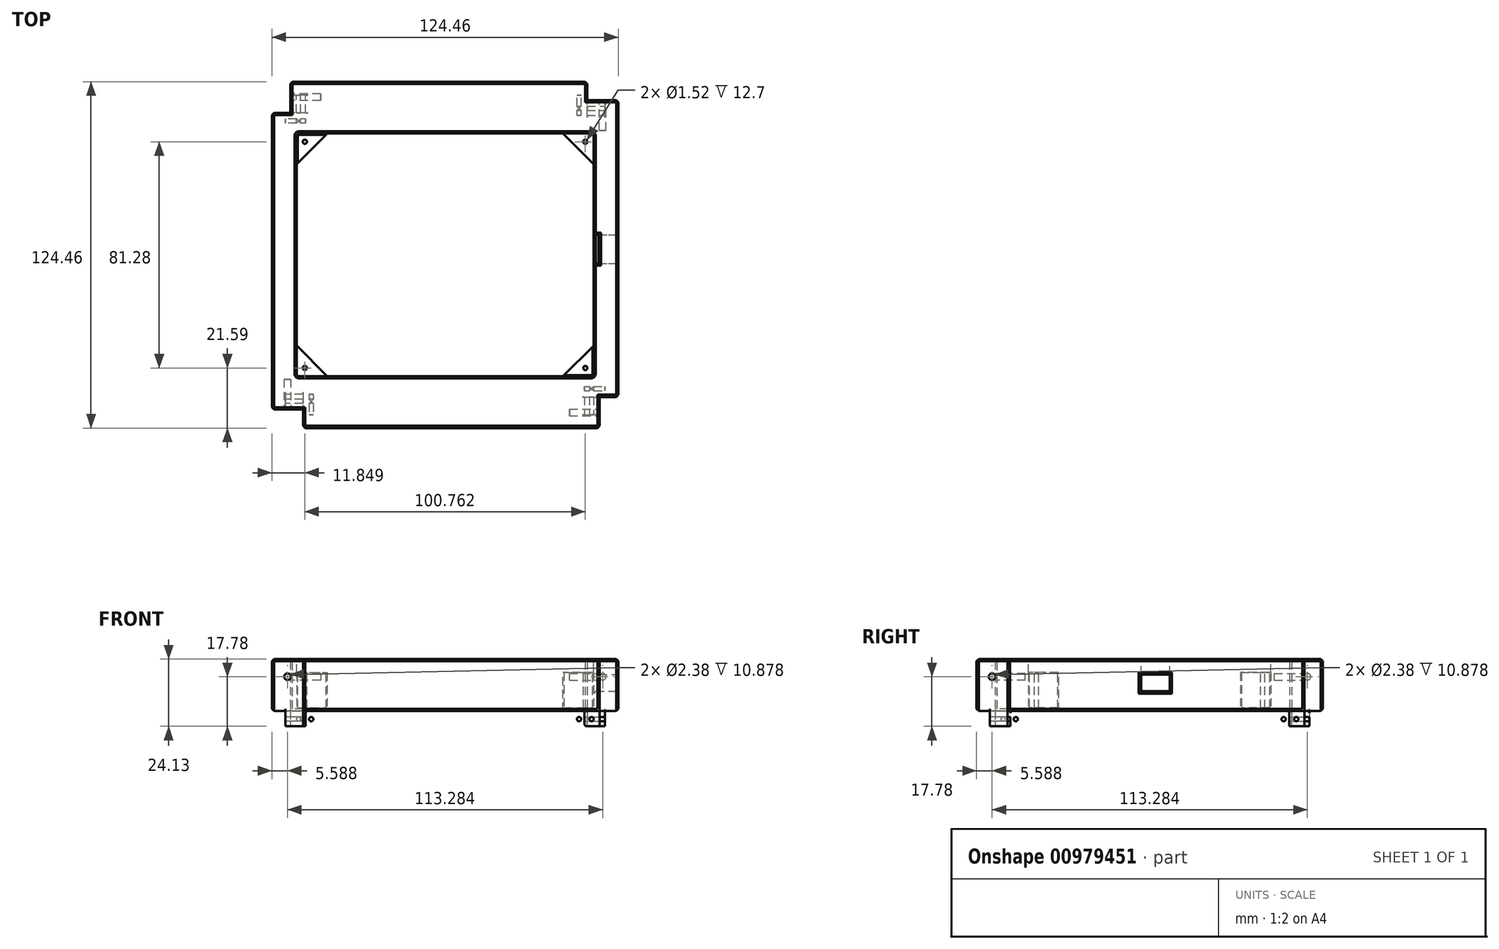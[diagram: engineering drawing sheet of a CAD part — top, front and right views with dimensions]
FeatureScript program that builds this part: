
annotation { "Feature Type Name" : "Feature", "Feature Type Description" : "" }
export const myFeature = defineFeature(function(context is Context, id is Id, definition is map)
    precondition{}
    {
        {
            var Q0;
            Q0=qCreatedBy(makeId("Top.planeOp"),FACE);
            var sketch = newSketch(context, id + "F0", { "sketchPlane" : qUnion([Q0])});
            skLineSegment(sketch, "E0.bottom", {"start": v(62.23, -62.23) * mm, "end": v(-62.23, -62.23) * mm});
            skLineSegment(sketch, "E0.top", {"start": v(62.23, 62.23) * mm, "end": v(-62.23, 62.23) * mm});
            skLineSegment(sketch, "E0.left", {"start": v(62.23, -62.23) * mm, "end": v(62.23, 62.23) * mm});
            skLineSegment(sketch, "E0.right", {"start": v(-62.23, -62.23) * mm, "end": v(-62.23, 62.23) * mm});
            skLineSegment(sketch, "E1.bottom", {"start": v(38.1, -38.1) * mm, "end": v(-38.1, -38.1) * mm});
            skLineSegment(sketch, "E1.top", {"start": v(38.1, 38.1) * mm, "end": v(-38.1, 38.1) * mm});
            skLineSegment(sketch, "E1.left", {"start": v(38.1, -38.1) * mm, "end": v(38.1, 38.1) * mm});
            skLineSegment(sketch, "E1.right", {"start": v(-38.1, -38.1) * mm, "end": v(-38.1, 38.1) * mm});
            skPoint(sketch, "E1.middle", {"position": v(0, 0) * mm});
            skSolve(sketch);
        }
        {
            var Q0;
            Q0=makeQuery(id+"F0.imprint","IMPRINT",FACE,{"disambiguationData":[TD([[makeQuery(id+"F0.imprint","IMPRINT",EDGE,{"derivedFrom":sQuery(id+"F0.wireOp",EDGE,"E0.bottom")}),-1.0]])]});
            extrude(context, id + "F1", {"entities" : qUnion([Q0]), "depth" : 124.46 * mm, "offsetDistance" : 25.4 * mm});
        }
        {
            var Q0;
            Q0=makeQuery(id+"F1.opExtrude","CAP_FACE",FACE,{"disambiguationData":[OSD([sQuery(id+"F0.wireOp",EDGE,"E0.bottom"),sQuery(id+"F0.wireOp",EDGE,"E0.top"),sQuery(id+"F0.wireOp",EDGE,"E0.left"),sQuery(id+"F0.wireOp",EDGE,"E0.right")])],"isStart":false});
            var sketch = newSketch(context, id + "F2", { "sketchPlane" : qUnion([Q0])});
            skLineSegment(sketch, "E2.bottom", {"start": v(-52.92, 43.18) * mm, "end": v(52.92, 43.18) * mm});
            skLineSegment(sketch, "E2.top", {"start": v(-52.92, -43.18) * mm, "end": v(52.92, -43.18) * mm});
            skLineSegment(sketch, "E2.left", {"start": v(-52.92, 43.18) * mm, "end": v(-52.92, -43.18) * mm});
            skLineSegment(sketch, "E2.right", {"start": v(52.92, 43.18) * mm, "end": v(52.92, -43.18) * mm});
            skPoint(sketch, "E2.middle", {"position": v(0, 0) * mm});
            skCircle(sketch, "E3", {"center": v(-50.38, -40.64) * mm, "radius": 0.76 * mm});
            skCircle(sketch, "E4.MirrorC", {"center": v(50.38, -40.64) * mm, "radius": 0.76 * mm});
            skCircle(sketch, "E5.MirrorC", {"center": v(-50.38, 40.64) * mm, "radius": 0.76 * mm});
            skCircle(sketch, "E6.MirrorC", {"center": v(50.38, 40.64) * mm, "radius": 0.76 * mm});
            skLineSegment(sketch, "E7.0", {"start": v(-53.32, 43.58) * mm, "end": v(-53.32, -43.58) * mm});
            skLineSegment(sketch, "E7.1", {"start": v(-53.32, 43.58) * mm, "end": v(53.32, 43.58) * mm});
            skLineSegment(sketch, "E7.2", {"start": v(53.32, 43.58) * mm, "end": v(53.32, -43.58) * mm});
            skLineSegment(sketch, "E7.3", {"start": v(-53.32, -43.58) * mm, "end": v(53.32, -43.58) * mm});
            skLineSegment(sketch, "E8.top", {"start": v(53.32, -38.1) * mm, "end": v(47.84, -38.1) * mm});
            skLineSegment(sketch, "E8.right", {"start": v(47.84, -43.58) * mm, "end": v(47.84, -38.1) * mm});
            skLineSegment(sketch, "E9.MirrorCS", {"start": v(47.84, 43.58) * mm, "end": v(47.84, 38.1) * mm});
            skLineSegment(sketch, "E10.MirrorCS", {"start": v(53.32, 38.1) * mm, "end": v(47.84, 38.1) * mm});
            skLineSegment(sketch, "E11.MirrorCS", {"start": v(-53.32, -38.1) * mm, "end": v(-47.84, -38.1) * mm});
            skLineSegment(sketch, "E12.MirrorCS", {"start": v(-47.84, -43.58) * mm, "end": v(-47.84, -38.1) * mm});
            skLineSegment(sketch, "E13.MirrorCS", {"start": v(-53.32, 38.1) * mm, "end": v(-47.84, 38.1) * mm});
            skLineSegment(sketch, "E14.MirrorCS", {"start": v(-47.84, 43.58) * mm, "end": v(-47.84, 38.1) * mm});
            skLineSegment(sketch, "E15.MirrorCS", {"start": v(51.04, 6.8) * mm, "end": v(54.8, 6.8) * mm});
            skLineSegment(sketch, "E16.MirrorCS", {"start": v(51.04, -3.13) * mm, "end": v(55.2, -3.13) * mm});
            skLineSegment(sketch, "E17.MirrorCS", {"start": v(51.04, -2.73) * mm, "end": v(54.8, -2.73) * mm});
            skLineSegment(sketch, "E18.MirrorCS", {"start": v(55.2, 7.2) * mm, "end": v(55.2, -3.13) * mm});
            skLineSegment(sketch, "E19.MirrorCS", {"start": v(51.04, 7.2) * mm, "end": v(55.2, 7.2) * mm});
            skLineSegment(sketch, "E20.MirrorCS", {"start": v(54.8, 6.8) * mm, "end": v(54.8, -2.73) * mm});
            skPoint(sketch, "E21.MirrorP", {"position": v(52.92, 2.03) * mm});
            skLineSegment(sketch, "E22.bottom", {"start": v(-62.23, -62.23) * mm, "end": v(62.23, -62.23) * mm});
            skLineSegment(sketch, "E22.top", {"start": v(-62.23, 62.23) * mm, "end": v(62.23, 62.23) * mm});
            skLineSegment(sketch, "E22.left", {"start": v(-62.23, -62.23) * mm, "end": v(-62.23, 62.23) * mm});
            skLineSegment(sketch, "E22.right", {"start": v(62.23, -62.23) * mm, "end": v(62.23, 62.23) * mm});
            skSolve(sketch);
        }
        {
            var Q0;
            Q0=makeQuery(id+"F2.imprint","IMPRINT",FACE,{"disambiguationData":[TD([[makeQuery(id+"F2.imprint","IMPRINT",EDGE,{"derivedFrom":sQuery(id+"F2.wireOp",EDGE,"E3")}),-1.0]])]});
            var Q1;
            {var subQ5=sQuery(id+"F2.wireOp",EDGE,"E2.left");var subQ6=sQuery(id+"F2.wireOp",EDGE,"E2.top");var subQ7=makeQuery(id+"F2.imprint","INTERSECT",VERTEX,{"derivedFrom":[subQ6,subQ5]});Q1=makeQuery(id+"F2.imprint","IMPRINT",FACE,{"disambiguationData":[TD([[makeQuery(id+"F2.imprint","IMPRINT",EDGE,{"disambiguationData":[TD([[subQ7,-1.0]])],"derivedFrom":subQ6}),-1.0]])]});}
            var Q2;
            {var subQ7=sQuery(id+"F2.wireOp",EDGE,"E2.right");var subQ8=sQuery(id+"F2.wireOp",EDGE,"E2.top");var subQ9=makeQuery(id+"F2.imprint","INTERSECT",VERTEX,{"derivedFrom":[subQ8,subQ7]});Q2=makeQuery(id+"F2.imprint","IMPRINT",FACE,{"disambiguationData":[TD([[makeQuery(id+"F2.imprint","IMPRINT",EDGE,{"disambiguationData":[TD([[subQ9,1.0]])],"derivedFrom":subQ8}),-1.0]])]});}
            var Q3;
            Q3=makeQuery(id+"F2.imprint","IMPRINT",FACE,{"disambiguationData":[TD([[makeQuery(id+"F2.imprint","IMPRINT",EDGE,{"derivedFrom":sQuery(id+"F2.wireOp",EDGE,"E4.MirrorC")}),1.0]])]});
            var Q4;
            {var subQ7=sQuery(id+"F2.wireOp",EDGE,"E2.right");var subQ8=sQuery(id+"F2.wireOp",EDGE,"E2.bottom");var subQ9=makeQuery(id+"F2.imprint","INTERSECT",VERTEX,{"derivedFrom":[subQ8,subQ7]});Q4=makeQuery(id+"F2.imprint","IMPRINT",FACE,{"disambiguationData":[TD([[makeQuery(id+"F2.imprint","IMPRINT",EDGE,{"disambiguationData":[TD([[subQ9,1.0]])],"derivedFrom":subQ8}),1.0]])]});}
            var Q5;
            Q5=makeQuery(id+"F2.imprint","IMPRINT",FACE,{"disambiguationData":[TD([[makeQuery(id+"F2.imprint","IMPRINT",EDGE,{"derivedFrom":sQuery(id+"F2.wireOp",EDGE,"E6.MirrorC")}),-1.0]])]});
            var Q6;
            {var subQ5=sQuery(id+"F2.wireOp",EDGE,"E2.left");var subQ6=sQuery(id+"F2.wireOp",EDGE,"E2.bottom");var subQ7=makeQuery(id+"F2.imprint","INTERSECT",VERTEX,{"derivedFrom":[subQ6,subQ5]});Q6=makeQuery(id+"F2.imprint","IMPRINT",FACE,{"disambiguationData":[TD([[makeQuery(id+"F2.imprint","IMPRINT",EDGE,{"disambiguationData":[TD([[subQ7,-1.0]])],"derivedFrom":subQ6}),1.0]])]});}
            var Q7;
            Q7=makeQuery(id+"F2.imprint","IMPRINT",FACE,{"disambiguationData":[TD([[makeQuery(id+"F2.imprint","IMPRINT",EDGE,{"derivedFrom":sQuery(id+"F2.wireOp",EDGE,"E5.MirrorC")}),1.0]])]});
            extrude(context, id + "F3", {"entities" : qUnion([Q0, Q1, Q2, Q3, Q4, Q5, Q6, Q7]), "operationType" : NewBodyOperationType.REMOVE, "oppositeDirection" : true, "depth" : 4.83 * mm, "offsetDistance" : 25.4 * mm});
        }
        {
            var Q0;
            {var subQ20=sQuery(id+"F2.wireOp",EDGE,"E2.bottom");var subQ22=sQuery(id+"F2.wireOp",EDGE,"E14.MirrorCS");var subQ23=makeQuery(id+"F2.imprint","INTERSECT",VERTEX,{"derivedFrom":[subQ20,subQ22]});Q0=makeQuery(id+"F2.imprint","IMPRINT",FACE,{"disambiguationData":[TD([[makeQuery(id+"F2.imprint","IMPRINT",EDGE,{"disambiguationData":[TD([[subQ23,-1.0]])],"derivedFrom":subQ20}),-1.0]])]});}
            var Q1;
            {var subQ0=sQuery(id+"F2.wireOp",EDGE,"E14.MirrorCS");var subQ1=sQuery(id+"F2.wireOp",EDGE,"E2.bottom");var subQ2=makeQuery(id+"F2.imprint","INTERSECT",VERTEX,{"derivedFrom":[subQ1,subQ0]});Q1=makeQuery(id+"F2.imprint","IMPRINT",FACE,{"disambiguationData":[TD([[makeQuery(id+"F2.imprint","IMPRINT",EDGE,{"disambiguationData":[TD([[subQ2,-1.0]])],"derivedFrom":subQ1}),1.0]])]});}
            var Q2;
            {var subQ0=sQuery(id+"F2.wireOp",EDGE,"59694670-6818-448a-b48b-58002c6f26f5.2");var subQ1=sQuery(id+"F2.wireOp",EDGE,"E2.left");var subQ2=makeQuery(id+"F2.imprint","INTERSECT",VERTEX,{"derivedFrom":[subQ1,subQ0]});Q2=makeQuery(id+"F2.imprint","IMPRINT",FACE,{"disambiguationData":[TD([[makeQuery(id+"F2.imprint","IMPRINT",EDGE,{"disambiguationData":[TD([[subQ2,1.0]])],"derivedFrom":subQ1}),-1.0]])]});}
            var Q3;
            {var subQ0=sQuery(id+"F2.wireOp",EDGE,"E10.MirrorCS");var subQ1=sQuery(id+"F2.wireOp",EDGE,"E2.right");var subQ2=makeQuery(id+"F2.imprint","INTERSECT",VERTEX,{"derivedFrom":[subQ1,subQ0]});Q3=makeQuery(id+"F2.imprint","IMPRINT",FACE,{"disambiguationData":[TD([[makeQuery(id+"F2.imprint","IMPRINT",EDGE,{"disambiguationData":[TD([[subQ2,-1.0]])],"derivedFrom":subQ1}),1.0]])]});}
            var Q4;
            {var subQ0=sQuery(id+"F2.wireOp",EDGE,"E12.MirrorCS");var subQ1=sQuery(id+"F2.wireOp",EDGE,"E2.top");var subQ2=makeQuery(id+"F2.imprint","INTERSECT",VERTEX,{"derivedFrom":[subQ1,subQ0]});Q4=makeQuery(id+"F2.imprint","IMPRINT",FACE,{"disambiguationData":[TD([[makeQuery(id+"F2.imprint","IMPRINT",EDGE,{"disambiguationData":[TD([[subQ2,-1.0]])],"derivedFrom":subQ1}),-1.0]])]});}
            var Q5;
            {var subQ0=sQuery(id+"F2.wireOp",EDGE,"01Z94Qzt-EJPi-t4h5-vXe4-wsMJar4ZymQo.bottom");var subQ1=sQuery(id+"F2.wireOp",EDGE,"E2.left");var subQ2=makeQuery(id+"F2.imprint","INTERSECT",VERTEX,{"derivedFrom":[subQ1,subQ0]});Q5=makeQuery(id+"F2.imprint","IMPRINT",FACE,{"disambiguationData":[TD([[makeQuery(id+"F2.imprint","IMPRINT",EDGE,{"disambiguationData":[TD([[subQ2,-1.0]])],"derivedFrom":subQ1}),-1.0]])]});}
            var Q6;
            {var subQ0=sQuery(id+"F2.wireOp",EDGE,"59694670-6818-448a-b48b-58002c6f26f5.2");var subQ1=sQuery(id+"F2.wireOp",EDGE,"E2.left");var subQ2=makeQuery(id+"F2.imprint","INTERSECT",VERTEX,{"derivedFrom":[subQ1,subQ0]});Q6=makeQuery(id+"F2.imprint","IMPRINT",FACE,{"disambiguationData":[TD([[makeQuery(id+"F2.imprint","IMPRINT",EDGE,{"disambiguationData":[TD([[subQ2,-1.0]])],"derivedFrom":subQ1}),-1.0]])]});}
            var Q7;
            {var subQ0=sQuery(id+"F2.wireOp",EDGE,"01Z94Qzt-EJPi-t4h5-vXe4-wsMJar4ZymQo.top");var subQ1=sQuery(id+"F2.wireOp",EDGE,"E2.left");var subQ2=makeQuery(id+"F2.imprint","INTERSECT",VERTEX,{"derivedFrom":[subQ1,subQ0]});Q7=makeQuery(id+"F2.imprint","IMPRINT",FACE,{"disambiguationData":[TD([[makeQuery(id+"F2.imprint","IMPRINT",EDGE,{"disambiguationData":[TD([[subQ2,-1.0]])],"derivedFrom":subQ1}),-1.0]])]});}
            var Q8;
            {var subQ0=sQuery(id+"F2.wireOp",EDGE,"59694670-6818-448a-b48b-58002c6f26f5.0");var subQ1=sQuery(id+"F2.wireOp",EDGE,"E2.left");var subQ2=makeQuery(id+"F2.imprint","INTERSECT",VERTEX,{"derivedFrom":[subQ1,subQ0]});Q8=makeQuery(id+"F2.imprint","IMPRINT",FACE,{"disambiguationData":[TD([[makeQuery(id+"F2.imprint","IMPRINT",EDGE,{"disambiguationData":[TD([[subQ2,-1.0]])],"derivedFrom":subQ1}),-1.0]])]});}
            var Q9;
            {var subQ0=sQuery(id+"F2.wireOp",EDGE,"E19.MirrorCS");var subQ1=sQuery(id+"F2.wireOp",EDGE,"E2.right");var subQ2=makeQuery(id+"F2.imprint","INTERSECT",VERTEX,{"derivedFrom":[subQ1,subQ0]});Q9=makeQuery(id+"F2.imprint","IMPRINT",FACE,{"disambiguationData":[TD([[makeQuery(id+"F2.imprint","IMPRINT",EDGE,{"disambiguationData":[TD([[subQ2,-1.0]])],"derivedFrom":subQ1}),1.0]])]});}
            var Q10;
            {var subQ0=sQuery(id+"F2.wireOp",EDGE,"E15.MirrorCS");var subQ1=sQuery(id+"F2.wireOp",EDGE,"E2.right");var subQ2=makeQuery(id+"F2.imprint","INTERSECT",VERTEX,{"derivedFrom":[subQ1,subQ0]});Q10=makeQuery(id+"F2.imprint","IMPRINT",FACE,{"disambiguationData":[TD([[makeQuery(id+"F2.imprint","IMPRINT",EDGE,{"disambiguationData":[TD([[subQ2,-1.0]])],"derivedFrom":subQ1}),1.0]])]});}
            var Q11;
            {var subQ0=sQuery(id+"F2.wireOp",EDGE,"E17.MirrorCS");var subQ1=sQuery(id+"F2.wireOp",EDGE,"E2.right");var subQ2=makeQuery(id+"F2.imprint","INTERSECT",VERTEX,{"derivedFrom":[subQ1,subQ0]});Q11=makeQuery(id+"F2.imprint","IMPRINT",FACE,{"disambiguationData":[TD([[makeQuery(id+"F2.imprint","IMPRINT",EDGE,{"disambiguationData":[TD([[subQ2,-1.0]])],"derivedFrom":subQ1}),1.0]])]});}
            var Q12;
            {var subQ0=sQuery(id+"F2.wireOp",EDGE,"E16.MirrorCS");var subQ1=sQuery(id+"F2.wireOp",EDGE,"E2.right");var subQ2=makeQuery(id+"F2.imprint","INTERSECT",VERTEX,{"derivedFrom":[subQ1,subQ0]});Q12=makeQuery(id+"F2.imprint","IMPRINT",FACE,{"disambiguationData":[TD([[makeQuery(id+"F2.imprint","IMPRINT",EDGE,{"disambiguationData":[TD([[subQ2,-1.0]])],"derivedFrom":subQ1}),1.0]])]});}
            extrude(context, id + "F4", {"entities" : qUnion([Q0, Q1, Q2, Q3, Q4, Q5, Q6, Q7, Q8, Q9, Q10, Q11, Q12]), "operationType" : NewBodyOperationType.REMOVE, "oppositeDirection" : true, "depth" : 25.4 * mm, "offsetDistance" : 25.4 * mm});
        }
        {
            var Q0;
            Q0=makeQuery(id+"F1.opExtrude","SWEPT_FACE",FACE,{"disambiguationData":[OSD([sQuery(id+"F0.wireOp",EDGE,"E0.bottom")])]});
            var sketch = newSketch(context, id + "F5", { "sketchPlane" : qUnion([Q0])});
            skPoint(sketch, "E23.middle", {"position": v(2.26, 62.23) * mm});
            skCircle(sketch, "E24", {"center": v(-48.12, 21.6) * mm, "radius": 0.76 * mm});
            skCircle(sketch, "E25.MirrorC", {"center": v(52.64, 21.6) * mm, "radius": 0.76 * mm});
            skCircle(sketch, "E26.MirrorC", {"center": v(-48.12, 102.87) * mm, "radius": 0.76 * mm});
            skCircle(sketch, "E27.MirrorC", {"center": v(52.64, 102.87) * mm, "radius": 0.76 * mm});
            skLineSegment(sketch, "E28.0", {"start": v(-51.05, 105.8) * mm, "end": v(-51.05, 18.65) * mm});
            skLineSegment(sketch, "E28.1", {"start": v(-51.05, 105.8) * mm, "end": v(55.58, 105.8) * mm});
            skLineSegment(sketch, "E28.2", {"start": v(55.58, 105.8) * mm, "end": v(55.58, 18.65) * mm});
            skLineSegment(sketch, "E28.3", {"start": v(-51.05, 18.65) * mm, "end": v(55.58, 18.65) * mm});
            skLineSegment(sketch, "E29.top", {"start": v(55.58, 24.13) * mm, "end": v(50.1, 24.13) * mm});
            skLineSegment(sketch, "E29.right", {"start": v(50.1, 18.65) * mm, "end": v(50.1, 24.13) * mm});
            skLineSegment(sketch, "E30.MirrorCS", {"start": v(50.1, 105.8) * mm, "end": v(50.1, 100.33) * mm});
            skLineSegment(sketch, "E31.MirrorCS", {"start": v(55.58, 100.33) * mm, "end": v(50.1, 100.33) * mm});
            skLineSegment(sketch, "E32.MirrorCS", {"start": v(-51.05, 24.13) * mm, "end": v(-45.58, 24.13) * mm});
            skLineSegment(sketch, "E33.MirrorCS", {"start": v(-45.58, 18.65) * mm, "end": v(-45.58, 24.13) * mm});
            skLineSegment(sketch, "E34.MirrorCS", {"start": v(-51.05, 100.33) * mm, "end": v(-45.58, 100.33) * mm});
            skLineSegment(sketch, "E35.MirrorCS", {"start": v(-45.58, 105.8) * mm, "end": v(-45.58, 100.33) * mm});
            skLineSegment(sketch, "E36.MirrorCS", {"start": v(53.3, 59.1) * mm, "end": v(57.46, 59.1) * mm});
            skLineSegment(sketch, "E37.MirrorCS", {"start": v(57.46, 69.42) * mm, "end": v(57.46, 59.1) * mm});
            skLineSegment(sketch, "E38.MirrorCS", {"start": v(53.3, 69.42) * mm, "end": v(57.46, 69.42) * mm});
            skPoint(sketch, "E39.MirrorP", {"position": v(55.18, 64.26) * mm});
            skPoint(sketch, "E40", {"position": v(-62.23, 62.23) * mm});
            skLineSegment(sketch, "E41.bottom", {"start": v(-62.23, 0) * mm, "end": v(62.23, 0) * mm});
            skLineSegment(sketch, "E41.top", {"start": v(-62.23, 124.46) * mm, "end": v(62.23, 124.46) * mm});
            skLineSegment(sketch, "E41.left", {"start": v(-62.23, 0) * mm, "end": v(-62.23, 124.46) * mm});
            skLineSegment(sketch, "E41.right", {"start": v(59.41, 0) * mm, "end": v(59.41, 124.46) * mm});
            skLineSegment(sketch, "E42.bottom", {"start": v(-62.23, 59.1) * mm, "end": v(-51.05, 59.1) * mm});
            skLineSegment(sketch, "E42.top", {"start": v(-62.23, 69.42) * mm, "end": v(-51.05, 69.42) * mm});
            skLineSegment(sketch, "E42.left", {"start": v(-62.23, 59.1) * mm, "end": v(-62.23, 69.42) * mm});
            skLineSegment(sketch, "E42.right", {"start": v(-51.05, 59.1) * mm, "end": v(-51.05, 69.42) * mm});
            skLineSegment(sketch, "E43", {"start": v(-56.25, 69.42) * mm, "end": v(-56.25, 59.1) * mm});
            skLineSegment(sketch, "E44", {"start": v(-45.58, 24.13) * mm, "end": v(50.1, 24.13) * mm});
            skLineSegment(sketch, "E45.bottom", {"start": v(-62.23, 0) * mm, "end": v(-56.64, 0) * mm});
            skLineSegment(sketch, "E45.top", {"start": v(-62.23, 6.35) * mm, "end": v(-56.64, 6.35) * mm});
            skLineSegment(sketch, "E45.left", {"start": v(-62.23, 0) * mm, "end": v(-62.23, 6.35) * mm});
            skLineSegment(sketch, "E45.right", {"start": v(-56.64, 0) * mm, "end": v(-56.64, 6.35) * mm});
            skLineSegment(sketch, "E46.bottom", {"start": v(-62.23, 124.46) * mm, "end": v(-56.64, 124.46) * mm});
            skLineSegment(sketch, "E46.top", {"start": v(-62.23, 118.11) * mm, "end": v(-56.64, 118.11) * mm});
            skLineSegment(sketch, "E46.left", {"start": v(-62.23, 124.46) * mm, "end": v(-62.23, 118.11) * mm});
            skLineSegment(sketch, "E46.right", {"start": v(-56.64, 124.46) * mm, "end": v(-56.64, 118.11) * mm});
            skCircle(sketch, "E47", {"center": v(-56.64, 118.11) * mm, "radius": 1.2 * mm});
            skCircle(sketch, "E48", {"center": v(-56.64, 6.35) * mm, "radius": 1.2 * mm});
            skSolve(sketch);
        }
        {
            var Q0;
            Q0=makeQuery(id+"F1.opExtrude","SWEPT_FACE",FACE,{"disambiguationData":[OSD([sQuery(id+"F0.wireOp",EDGE,"E0.left")])]});
            var sketch = newSketch(context, id + "F6", { "sketchPlane" : qUnion([Q0])});
            skPoint(sketch, "E49.middle", {"position": v(2.26, 62.23) * mm});
            skCircle(sketch, "E50", {"center": v(-48.12, 21.59) * mm, "radius": 0.76 * mm});
            skCircle(sketch, "E51.MirrorC", {"center": v(52.64, 21.59) * mm, "radius": 0.76 * mm});
            skCircle(sketch, "E52.MirrorC", {"center": v(-48.12, 102.87) * mm, "radius": 0.76 * mm});
            skCircle(sketch, "E53.MirrorC", {"center": v(52.64, 102.87) * mm, "radius": 0.76 * mm});
            skLineSegment(sketch, "E54.0", {"start": v(-51.05, 105.8) * mm, "end": v(-51.05, 18.65) * mm});
            skLineSegment(sketch, "E54.1", {"start": v(-51.05, 105.8) * mm, "end": v(55.58, 105.8) * mm});
            skLineSegment(sketch, "E54.2", {"start": v(55.58, 105.8) * mm, "end": v(55.58, 18.65) * mm});
            skLineSegment(sketch, "E54.3", {"start": v(-51.05, 18.65) * mm, "end": v(55.58, 18.65) * mm});
            skLineSegment(sketch, "E55.top", {"start": v(55.58, 24.13) * mm, "end": v(50.1, 24.13) * mm});
            skLineSegment(sketch, "E55.right", {"start": v(50.1, 18.65) * mm, "end": v(50.1, 24.13) * mm});
            skLineSegment(sketch, "E56.MirrorCS", {"start": v(50.1, 105.8) * mm, "end": v(50.1, 100.33) * mm});
            skLineSegment(sketch, "E57.MirrorCS", {"start": v(55.58, 100.33) * mm, "end": v(50.1, 100.33) * mm});
            skLineSegment(sketch, "E58.MirrorCS", {"start": v(-51.05, 24.13) * mm, "end": v(-45.58, 24.13) * mm});
            skLineSegment(sketch, "E59.MirrorCS", {"start": v(-45.58, 18.65) * mm, "end": v(-45.58, 24.13) * mm});
            skLineSegment(sketch, "E60.MirrorCS", {"start": v(-51.05, 100.33) * mm, "end": v(-45.58, 100.33) * mm});
            skLineSegment(sketch, "E61.MirrorCS", {"start": v(-45.58, 105.8) * mm, "end": v(-45.58, 100.33) * mm});
            skLineSegment(sketch, "E62.MirrorCS", {"start": v(53.3, 59.1) * mm, "end": v(57.46, 59.1) * mm});
            skLineSegment(sketch, "E63.MirrorCS", {"start": v(57.46, 69.42) * mm, "end": v(57.46, 59.1) * mm});
            skLineSegment(sketch, "E64.MirrorCS", {"start": v(53.3, 69.42) * mm, "end": v(57.46, 69.42) * mm});
            skPoint(sketch, "E65.MirrorP", {"position": v(55.18, 64.26) * mm});
            skPoint(sketch, "E66", {"position": v(-62.23, 62.23) * mm});
            skLineSegment(sketch, "E67.bottom", {"start": v(-62.23, 0) * mm, "end": v(62.23, 0) * mm});
            skLineSegment(sketch, "E67.top", {"start": v(-62.23, 124.46) * mm, "end": v(62.23, 124.46) * mm});
            skLineSegment(sketch, "E67.left", {"start": v(-62.23, 0) * mm, "end": v(-62.23, 124.46) * mm});
            skLineSegment(sketch, "E67.right", {"start": v(62.23, 0) * mm, "end": v(62.23, 124.46) * mm});
            skLineSegment(sketch, "E68.bottom", {"start": v(-62.23, 59.1) * mm, "end": v(-51.05, 59.1) * mm});
            skLineSegment(sketch, "E68.top", {"start": v(-62.23, 69.42) * mm, "end": v(-51.05, 69.42) * mm});
            skLineSegment(sketch, "E68.left", {"start": v(-62.23, 59.1) * mm, "end": v(-62.23, 69.42) * mm});
            skLineSegment(sketch, "E68.right", {"start": v(-51.05, 59.1) * mm, "end": v(-51.05, 69.42) * mm});
            skLineSegment(sketch, "E69", {"start": v(-56.25, 69.42) * mm, "end": v(-56.25, 59.1) * mm});
            skPoint(sketch, "E70", {"position": v(-0.1, 124.06) * mm});
            skLineSegment(sketch, "E71.bottom", {"start": v(-3.13, 124.46) * mm, "end": v(-3.13, 112.89) * mm});
            skLineSegment(sketch, "E71.top", {"start": v(7.2, 124.46) * mm, "end": v(7.2, 112.89) * mm});
            skLineSegment(sketch, "E71.left", {"start": v(-3.13, 124.46) * mm, "end": v(7.2, 124.46) * mm});
            skLineSegment(sketch, "E71.right", {"start": v(-3.13, 112.89) * mm, "end": v(7.2, 112.89) * mm});
            skLineSegment(sketch, "E72", {"start": v(7.2, 118.88) * mm, "end": v(-3.13, 118.88) * mm});
            skLineSegment(sketch, "E73", {"start": v(-45.58, 24.13) * mm, "end": v(50.1, 24.13) * mm});
            skLineSegment(sketch, "E74.bottom", {"start": v(-62.23, 0) * mm, "end": v(-56.64, 0) * mm});
            skLineSegment(sketch, "E74.top", {"start": v(-62.23, 6.35) * mm, "end": v(-56.64, 6.35) * mm});
            skLineSegment(sketch, "E74.left", {"start": v(-62.23, 0) * mm, "end": v(-62.23, 6.35) * mm});
            skLineSegment(sketch, "E74.right", {"start": v(-56.64, 0) * mm, "end": v(-56.64, 6.35) * mm});
            skLineSegment(sketch, "E75.bottom", {"start": v(-62.23, 124.46) * mm, "end": v(-56.64, 124.46) * mm});
            skLineSegment(sketch, "E75.top", {"start": v(-62.23, 118.11) * mm, "end": v(-56.64, 118.11) * mm});
            skLineSegment(sketch, "E75.left", {"start": v(-62.23, 124.46) * mm, "end": v(-62.23, 118.11) * mm});
            skLineSegment(sketch, "E75.right", {"start": v(-56.64, 124.46) * mm, "end": v(-56.64, 118.11) * mm});
            skCircle(sketch, "E76", {"center": v(-56.64, 118.11) * mm, "radius": 1.2 * mm});
            skCircle(sketch, "E77", {"center": v(-56.64, 6.35) * mm, "radius": 1.2 * mm});
            skSolve(sketch);
        }
        {
            var Q0;
            Q0=makeQuery(id+"F1.opExtrude","SWEPT_FACE",FACE,{"disambiguationData":[OSD([sQuery(id+"F0.wireOp",EDGE,"E0.top")])]});
            var sketch = newSketch(context, id + "F7", { "sketchPlane" : qUnion([Q0])});
            skPoint(sketch, "E78.middle", {"position": v(2.26, 62.23) * mm});
            skCircle(sketch, "E79", {"center": v(-48.12, 21.59) * mm, "radius": 0.76 * mm});
            skCircle(sketch, "E80.MirrorC", {"center": v(52.64, 21.59) * mm, "radius": 0.76 * mm});
            skCircle(sketch, "E81.MirrorC", {"center": v(-48.12, 102.87) * mm, "radius": 0.76 * mm});
            skCircle(sketch, "E82.MirrorC", {"center": v(52.64, 102.87) * mm, "radius": 0.76 * mm});
            skLineSegment(sketch, "E83.0", {"start": v(-51.05, 105.8) * mm, "end": v(-51.05, 18.65) * mm});
            skLineSegment(sketch, "E83.1", {"start": v(-51.05, 105.8) * mm, "end": v(55.58, 105.8) * mm});
            skLineSegment(sketch, "E83.2", {"start": v(55.58, 105.8) * mm, "end": v(55.58, 18.65) * mm});
            skLineSegment(sketch, "E83.3", {"start": v(-51.05, 18.65) * mm, "end": v(55.58, 18.65) * mm});
            skLineSegment(sketch, "E84.top", {"start": v(55.58, 24.13) * mm, "end": v(50.1, 24.13) * mm});
            skLineSegment(sketch, "E84.right", {"start": v(50.1, 18.65) * mm, "end": v(50.1, 24.13) * mm});
            skLineSegment(sketch, "E85.MirrorCS", {"start": v(50.1, 105.8) * mm, "end": v(50.1, 100.33) * mm});
            skLineSegment(sketch, "E86.MirrorCS", {"start": v(55.58, 100.33) * mm, "end": v(50.1, 100.33) * mm});
            skLineSegment(sketch, "E87.MirrorCS", {"start": v(-51.05, 24.13) * mm, "end": v(-45.58, 24.13) * mm});
            skLineSegment(sketch, "E88.MirrorCS", {"start": v(-45.58, 18.65) * mm, "end": v(-45.58, 24.13) * mm});
            skLineSegment(sketch, "E89.MirrorCS", {"start": v(-51.05, 100.33) * mm, "end": v(-45.58, 100.33) * mm});
            skLineSegment(sketch, "E90.MirrorCS", {"start": v(-45.58, 105.8) * mm, "end": v(-45.58, 100.33) * mm});
            skLineSegment(sketch, "E91.MirrorCS", {"start": v(53.3, 59.1) * mm, "end": v(57.46, 59.1) * mm});
            skLineSegment(sketch, "E92.MirrorCS", {"start": v(57.46, 69.42) * mm, "end": v(57.46, 59.1) * mm});
            skLineSegment(sketch, "E93.MirrorCS", {"start": v(53.3, 69.42) * mm, "end": v(57.46, 69.42) * mm});
            skPoint(sketch, "E94.MirrorP", {"position": v(55.18, 64.26) * mm});
            skPoint(sketch, "E95", {"position": v(-62.23, 62.23) * mm});
            skLineSegment(sketch, "E96.bottom", {"start": v(-62.23, 0) * mm, "end": v(62.23, 0) * mm});
            skLineSegment(sketch, "E96.top", {"start": v(-62.23, 124.46) * mm, "end": v(62.23, 124.46) * mm});
            skLineSegment(sketch, "E96.left", {"start": v(-62.23, 0) * mm, "end": v(-62.23, 124.46) * mm});
            skLineSegment(sketch, "E96.right", {"start": v(62.23, 0) * mm, "end": v(62.23, 124.46) * mm});
            skLineSegment(sketch, "E97.bottom", {"start": v(-62.23, 59.1) * mm, "end": v(-51.05, 59.1) * mm});
            skLineSegment(sketch, "E97.top", {"start": v(-62.23, 69.42) * mm, "end": v(-51.05, 69.42) * mm});
            skLineSegment(sketch, "E97.left", {"start": v(-62.23, 59.1) * mm, "end": v(-62.23, 69.42) * mm});
            skLineSegment(sketch, "E97.right", {"start": v(-51.05, 59.1) * mm, "end": v(-51.05, 69.42) * mm});
            skLineSegment(sketch, "E98", {"start": v(-56.25, 69.42) * mm, "end": v(-56.25, 59.1) * mm});
            skLineSegment(sketch, "E99", {"start": v(-45.58, 24.13) * mm, "end": v(50.1, 24.13) * mm});
            skLineSegment(sketch, "E100.bottom", {"start": v(-62.23, 0) * mm, "end": v(-56.64, 0) * mm});
            skLineSegment(sketch, "E100.top", {"start": v(-62.23, 6.35) * mm, "end": v(-56.64, 6.35) * mm});
            skLineSegment(sketch, "E100.left", {"start": v(-62.23, 0) * mm, "end": v(-62.23, 6.35) * mm});
            skLineSegment(sketch, "E100.right", {"start": v(-56.64, 0) * mm, "end": v(-56.64, 6.35) * mm});
            skLineSegment(sketch, "E101.bottom", {"start": v(-62.23, 124.46) * mm, "end": v(-56.64, 124.46) * mm});
            skLineSegment(sketch, "E101.top", {"start": v(-62.23, 118.11) * mm, "end": v(-56.64, 118.11) * mm});
            skLineSegment(sketch, "E101.left", {"start": v(-62.23, 124.46) * mm, "end": v(-62.23, 118.11) * mm});
            skLineSegment(sketch, "E101.right", {"start": v(-56.64, 124.46) * mm, "end": v(-56.64, 118.11) * mm});
            skCircle(sketch, "E102", {"center": v(-56.64, 118.11) * mm, "radius": 1.2 * mm});
            skCircle(sketch, "E103", {"center": v(-56.64, 6.35) * mm, "radius": 1.2 * mm});
            skSolve(sketch);
        }
        {
            var Q0;
            Q0=makeQuery(id+"F1.opExtrude","SWEPT_FACE",FACE,{"disambiguationData":[OSD([sQuery(id+"F0.wireOp",EDGE,"E0.right")])]});
            var sketch = newSketch(context, id + "F8", { "sketchPlane" : qUnion([Q0])});
            skPoint(sketch, "E104.middle", {"position": v(2.26, 62.23) * mm});
            skCircle(sketch, "E105", {"center": v(-48.12, 21.59) * mm, "radius": 0.76 * mm});
            skCircle(sketch, "E106.MirrorC", {"center": v(52.64, 21.59) * mm, "radius": 0.76 * mm});
            skCircle(sketch, "E107.MirrorC", {"center": v(-48.12, 102.87) * mm, "radius": 0.76 * mm});
            skCircle(sketch, "E108.MirrorC", {"center": v(52.64, 102.87) * mm, "radius": 0.76 * mm});
            skLineSegment(sketch, "E109.0", {"start": v(-51.05, 105.8) * mm, "end": v(-51.05, 18.65) * mm});
            skLineSegment(sketch, "E109.1", {"start": v(-51.05, 105.8) * mm, "end": v(55.58, 105.8) * mm});
            skLineSegment(sketch, "E109.2", {"start": v(55.58, 105.8) * mm, "end": v(55.58, 18.65) * mm});
            skLineSegment(sketch, "E109.3", {"start": v(-51.05, 18.65) * mm, "end": v(55.58, 18.65) * mm});
            skLineSegment(sketch, "E110.top", {"start": v(55.58, 24.13) * mm, "end": v(50.1, 24.13) * mm});
            skLineSegment(sketch, "E110.right", {"start": v(50.1, 18.65) * mm, "end": v(50.1, 24.13) * mm});
            skLineSegment(sketch, "E111.MirrorCS", {"start": v(50.1, 105.8) * mm, "end": v(50.1, 100.33) * mm});
            skLineSegment(sketch, "E112.MirrorCS", {"start": v(55.58, 100.33) * mm, "end": v(50.1, 100.33) * mm});
            skLineSegment(sketch, "E113.MirrorCS", {"start": v(-51.05, 24.13) * mm, "end": v(-45.58, 24.13) * mm});
            skLineSegment(sketch, "E114.MirrorCS", {"start": v(-45.58, 18.65) * mm, "end": v(-45.58, 24.13) * mm});
            skLineSegment(sketch, "E115.MirrorCS", {"start": v(-51.05, 100.33) * mm, "end": v(-45.58, 100.33) * mm});
            skLineSegment(sketch, "E116.MirrorCS", {"start": v(-45.58, 105.8) * mm, "end": v(-45.58, 100.33) * mm});
            skLineSegment(sketch, "E117.MirrorCS", {"start": v(53.3, 59.1) * mm, "end": v(57.46, 59.1) * mm});
            skLineSegment(sketch, "E118.MirrorCS", {"start": v(57.46, 69.42) * mm, "end": v(57.46, 59.1) * mm});
            skLineSegment(sketch, "E119.MirrorCS", {"start": v(53.3, 69.42) * mm, "end": v(57.46, 69.42) * mm});
            skPoint(sketch, "E120.MirrorP", {"position": v(55.18, 64.26) * mm});
            skPoint(sketch, "E121", {"position": v(-62.23, 62.23) * mm});
            skLineSegment(sketch, "E122.bottom", {"start": v(-62.23, 0) * mm, "end": v(62.23, 0) * mm});
            skLineSegment(sketch, "E122.top", {"start": v(-62.23, 124.46) * mm, "end": v(62.23, 124.46) * mm});
            skLineSegment(sketch, "E122.left", {"start": v(-62.23, 0) * mm, "end": v(-62.23, 124.46) * mm});
            skLineSegment(sketch, "E122.right", {"start": v(62.23, 0) * mm, "end": v(62.23, 124.46) * mm});
            skLineSegment(sketch, "E123.bottom", {"start": v(-62.23, 59.1) * mm, "end": v(-51.05, 59.1) * mm});
            skLineSegment(sketch, "E123.top", {"start": v(-62.23, 69.42) * mm, "end": v(-51.05, 69.42) * mm});
            skLineSegment(sketch, "E123.left", {"start": v(-62.23, 59.1) * mm, "end": v(-62.23, 69.42) * mm});
            skLineSegment(sketch, "E123.right", {"start": v(-51.05, 59.1) * mm, "end": v(-51.05, 69.42) * mm});
            skLineSegment(sketch, "E124", {"start": v(-56.25, 69.42) * mm, "end": v(-56.25, 59.1) * mm});
            skLineSegment(sketch, "E125", {"start": v(-45.58, 24.13) * mm, "end": v(50.1, 24.13) * mm});
            skLineSegment(sketch, "E126.bottom", {"start": v(-62.23, 0) * mm, "end": v(-56.64, 0) * mm});
            skLineSegment(sketch, "E126.top", {"start": v(-62.23, 6.35) * mm, "end": v(-56.64, 6.35) * mm});
            skLineSegment(sketch, "E126.left", {"start": v(-62.23, 0) * mm, "end": v(-62.23, 6.35) * mm});
            skLineSegment(sketch, "E126.right", {"start": v(-56.64, 0) * mm, "end": v(-56.64, 6.35) * mm});
            skLineSegment(sketch, "E127.bottom", {"start": v(-62.23, 124.46) * mm, "end": v(-56.64, 124.46) * mm});
            skLineSegment(sketch, "E127.top", {"start": v(-62.23, 118.11) * mm, "end": v(-56.64, 118.11) * mm});
            skLineSegment(sketch, "E127.left", {"start": v(-62.23, 124.46) * mm, "end": v(-62.23, 118.11) * mm});
            skLineSegment(sketch, "E127.right", {"start": v(-56.64, 124.46) * mm, "end": v(-56.64, 118.11) * mm});
            skCircle(sketch, "E128", {"center": v(-56.64, 118.11) * mm, "radius": 1.2 * mm});
            skCircle(sketch, "E129", {"center": v(-56.64, 6.35) * mm, "radius": 1.2 * mm});
            skSolve(sketch);
        }
        {
            var Q0;
            {var subQ2=sQuery(id+"F5.wireOp",EDGE,"E29.top");Q0=makeQuery(id+"F5.imprint","IMPRINT",FACE,{"disambiguationData":[TD([[makeQuery(id+"F5.imprint","IMPRINT",EDGE,{"derivedFrom":subQ2}),-1.0]])]});}
            var Q1;
            {var subQ0=sQuery(id+"F5.wireOp",EDGE,"E42.right");Q1=makeQuery(id+"F5.imprint","IMPRINT",FACE,{"disambiguationData":[TD([[makeQuery(id+"F5.imprint","IMPRINT",EDGE,{"derivedFrom":subQ0}),1.0]])]});}
            extrude(context, id + "F9", {"entities" : qUnion([Q0, Q1]), "operationType" : NewBodyOperationType.REMOVE, "oppositeDirection" : true, "depth" : 76.2 * mm, "offsetDistance" : 25.4 * mm});
        }
        {
            var Q0;
            {var subQ2=sQuery(id+"F8.wireOp",EDGE,"E110.top");Q0=makeQuery(id+"F8.imprint","IMPRINT",FACE,{"disambiguationData":[TD([[makeQuery(id+"F8.imprint","IMPRINT",EDGE,{"derivedFrom":subQ2}),-1.0]])]});}
            var Q1;
            {var subQ0=sQuery(id+"F8.wireOp",EDGE,"E123.right");Q1=makeQuery(id+"F8.imprint","IMPRINT",FACE,{"disambiguationData":[TD([[makeQuery(id+"F8.imprint","IMPRINT",EDGE,{"derivedFrom":subQ0}),1.0]])]});}
            extrude(context, id + "F10", {"entities" : qUnion([Q0, Q1]), "operationType" : NewBodyOperationType.REMOVE, "oppositeDirection" : true, "depth" : 76.2 * mm, "offsetDistance" : 25.4 * mm});
        }
        {
            var Q0;
            {var subQ2=sQuery(id+"F7.wireOp",EDGE,"E84.top");Q0=makeQuery(id+"F7.imprint","IMPRINT",FACE,{"disambiguationData":[TD([[makeQuery(id+"F7.imprint","IMPRINT",EDGE,{"derivedFrom":subQ2}),-1.0]])]});}
            var Q1;
            {var subQ0=sQuery(id+"F7.wireOp",EDGE,"E97.right");Q1=makeQuery(id+"F7.imprint","IMPRINT",FACE,{"disambiguationData":[TD([[makeQuery(id+"F7.imprint","IMPRINT",EDGE,{"derivedFrom":subQ0}),1.0]])]});}
            extrude(context, id + "F11", {"entities" : qUnion([Q0, Q1]), "operationType" : NewBodyOperationType.REMOVE, "oppositeDirection" : true, "depth" : 76.2 * mm, "offsetDistance" : 25.4 * mm});
        }
        {
            var Q0;
            {var subQ2=sQuery(id+"F6.wireOp",EDGE,"E55.top");Q0=makeQuery(id+"F6.imprint","IMPRINT",FACE,{"disambiguationData":[TD([[makeQuery(id+"F6.imprint","IMPRINT",EDGE,{"derivedFrom":subQ2}),-1.0]])]});}
            var Q1;
            {var subQ0=sQuery(id+"F6.wireOp",EDGE,"E68.right");Q1=makeQuery(id+"F6.imprint","IMPRINT",FACE,{"disambiguationData":[TD([[makeQuery(id+"F6.imprint","IMPRINT",EDGE,{"derivedFrom":subQ0}),1.0]])]});}
            var Q2;
            {var subQ0=sQuery(id+"F6.wireOp",EDGE,"E71.right");Q2=makeQuery(id+"F6.imprint","IMPRINT",FACE,{"disambiguationData":[TD([[makeQuery(id+"F6.imprint","IMPRINT",EDGE,{"derivedFrom":subQ0}),1.0]])]});}
            extrude(context, id + "F12", {"entities" : qUnion([Q0, Q1, Q2]), "operationType" : NewBodyOperationType.REMOVE, "oppositeDirection" : true, "depth" : 76.2 * mm, "offsetDistance" : 25.4 * mm});
        }
        {
            var Q0;
            Q0=makeQuery(id+"F5.imprint","IMPRINT",FACE,{"disambiguationData":[TD([[makeQuery(id+"F5.imprint","IMPRINT",EDGE,{"derivedFrom":sQuery(id+"F5.wireOp",EDGE,"E24")}),1.0]])]});
            var Q1;
            Q1=makeQuery(id+"F5.imprint","IMPRINT",FACE,{"disambiguationData":[TD([[makeQuery(id+"F5.imprint","IMPRINT",EDGE,{"derivedFrom":sQuery(id+"F5.wireOp",EDGE,"E25.MirrorC")}),-1.0]])]});
            var Q2;
            Q2=makeQuery(id+"F5.imprint","IMPRINT",FACE,{"disambiguationData":[TD([[makeQuery(id+"F5.imprint","IMPRINT",EDGE,{"derivedFrom":sQuery(id+"F5.wireOp",EDGE,"E27.MirrorC")}),1.0]])]});
            var Q3;
            Q3=makeQuery(id+"F5.imprint","IMPRINT",FACE,{"disambiguationData":[TD([[makeQuery(id+"F5.imprint","IMPRINT",EDGE,{"derivedFrom":sQuery(id+"F5.wireOp",EDGE,"E26.MirrorC")}),-1.0]])]});
            var Q4;
            {var subQ0=sQuery(id+"F5.wireOp",EDGE,"E46.right");var subQ1=sQuery(id+"F5.wireOp",EDGE,"E46.top");var subQ2=makeQuery(id+"F5.imprint","INTERSECT",VERTEX,{"derivedFrom":[subQ1,subQ0]});Q4=makeQuery(id+"F5.imprint","IMPRINT",FACE,{"disambiguationData":[TD([[makeQuery(id+"F5.imprint","IMPRINT",EDGE,{"disambiguationData":[TD([[subQ2,1.0]])],"derivedFrom":subQ1}),-1.0]])]});}
            var Q5;
            {var subQ0=sQuery(id+"F5.wireOp",EDGE,"E46.right");var subQ1=sQuery(id+"F5.wireOp",EDGE,"E46.top");var subQ2=makeQuery(id+"F5.imprint","INTERSECT",VERTEX,{"derivedFrom":[subQ1,subQ0]});Q5=makeQuery(id+"F5.imprint","IMPRINT",FACE,{"disambiguationData":[TD([[makeQuery(id+"F5.imprint","IMPRINT",EDGE,{"disambiguationData":[TD([[subQ2,1.0]])],"derivedFrom":subQ1}),1.0]])]});}
            var Q6;
            {var subQ0=sQuery(id+"F5.wireOp",EDGE,"E45.right");var subQ1=sQuery(id+"F5.wireOp",EDGE,"E45.top");var subQ2=makeQuery(id+"F5.imprint","INTERSECT",VERTEX,{"derivedFrom":[subQ1,subQ0]});Q6=makeQuery(id+"F5.imprint","IMPRINT",FACE,{"disambiguationData":[TD([[makeQuery(id+"F5.imprint","IMPRINT",EDGE,{"disambiguationData":[TD([[subQ2,1.0]])],"derivedFrom":subQ1}),1.0]])]});}
            var Q7;
            {var subQ0=sQuery(id+"F5.wireOp",EDGE,"E45.right");var subQ1=sQuery(id+"F5.wireOp",EDGE,"E45.top");var subQ2=makeQuery(id+"F5.imprint","INTERSECT",VERTEX,{"derivedFrom":[subQ1,subQ0]});Q7=makeQuery(id+"F5.imprint","IMPRINT",FACE,{"disambiguationData":[TD([[makeQuery(id+"F5.imprint","IMPRINT",EDGE,{"disambiguationData":[TD([[subQ2,1.0]])],"derivedFrom":subQ1}),-1.0]])]});}
            extrude(context, id + "F13", {"entities" : qUnion([Q0, Q1, Q2, Q3, Q4, Q5, Q6, Q7]), "operationType" : NewBodyOperationType.REMOVE, "oppositeDirection" : true, "depth" : 17.53 * mm, "offsetDistance" : 25.4 * mm});
        }
        {
            var Q0;
            Q0=makeQuery(id+"F6.imprint","IMPRINT",FACE,{"disambiguationData":[TD([[makeQuery(id+"F6.imprint","IMPRINT",EDGE,{"derivedFrom":sQuery(id+"F6.wireOp",EDGE,"E52.MirrorC")}),-1.0]])]});
            var Q1;
            Q1=makeQuery(id+"F6.imprint","IMPRINT",FACE,{"disambiguationData":[TD([[makeQuery(id+"F6.imprint","IMPRINT",EDGE,{"derivedFrom":sQuery(id+"F6.wireOp",EDGE,"E53.MirrorC")}),1.0]])]});
            var Q2;
            Q2=makeQuery(id+"F6.imprint","IMPRINT",FACE,{"disambiguationData":[TD([[makeQuery(id+"F6.imprint","IMPRINT",EDGE,{"derivedFrom":sQuery(id+"F6.wireOp",EDGE,"E51.MirrorC")}),-1.0]])]});
            var Q3;
            Q3=makeQuery(id+"F6.imprint","IMPRINT",FACE,{"disambiguationData":[TD([[makeQuery(id+"F6.imprint","IMPRINT",EDGE,{"derivedFrom":sQuery(id+"F6.wireOp",EDGE,"E50")}),1.0]])]});
            var Q4;
            {var subQ0=sQuery(id+"F6.wireOp",EDGE,"E74.right");var subQ1=sQuery(id+"F6.wireOp",EDGE,"E74.top");var subQ2=makeQuery(id+"F6.imprint","INTERSECT",VERTEX,{"derivedFrom":[subQ1,subQ0]});Q4=makeQuery(id+"F6.imprint","IMPRINT",FACE,{"disambiguationData":[TD([[makeQuery(id+"F6.imprint","IMPRINT",EDGE,{"disambiguationData":[TD([[subQ2,1.0]])],"derivedFrom":subQ1}),-1.0]])]});}
            var Q5;
            {var subQ0=sQuery(id+"F6.wireOp",EDGE,"E74.right");var subQ1=sQuery(id+"F6.wireOp",EDGE,"E74.top");var subQ2=makeQuery(id+"F6.imprint","INTERSECT",VERTEX,{"derivedFrom":[subQ1,subQ0]});Q5=makeQuery(id+"F6.imprint","IMPRINT",FACE,{"disambiguationData":[TD([[makeQuery(id+"F6.imprint","IMPRINT",EDGE,{"disambiguationData":[TD([[subQ2,1.0]])],"derivedFrom":subQ1}),1.0]])]});}
            var Q6;
            {var subQ0=sQuery(id+"F6.wireOp",EDGE,"E75.right");var subQ1=sQuery(id+"F6.wireOp",EDGE,"E75.top");var subQ2=makeQuery(id+"F6.imprint","INTERSECT",VERTEX,{"derivedFrom":[subQ1,subQ0]});Q6=makeQuery(id+"F6.imprint","IMPRINT",FACE,{"disambiguationData":[TD([[makeQuery(id+"F6.imprint","IMPRINT",EDGE,{"disambiguationData":[TD([[subQ2,1.0]])],"derivedFrom":subQ1}),1.0]])]});}
            var Q7;
            {var subQ0=sQuery(id+"F6.wireOp",EDGE,"E75.right");var subQ1=sQuery(id+"F6.wireOp",EDGE,"E75.top");var subQ2=makeQuery(id+"F6.imprint","INTERSECT",VERTEX,{"derivedFrom":[subQ1,subQ0]});Q7=makeQuery(id+"F6.imprint","IMPRINT",FACE,{"disambiguationData":[TD([[makeQuery(id+"F6.imprint","IMPRINT",EDGE,{"disambiguationData":[TD([[subQ2,1.0]])],"derivedFrom":subQ1}),-1.0]])]});}
            extrude(context, id + "F14", {"entities" : qUnion([Q0, Q1, Q2, Q3, Q4, Q5, Q6, Q7]), "operationType" : NewBodyOperationType.REMOVE, "oppositeDirection" : true, "depth" : 17.53 * mm, "offsetDistance" : 25.4 * mm});
        }
        {
            var Q0;
            Q0=makeQuery(id+"F7.imprint","IMPRINT",FACE,{"disambiguationData":[TD([[makeQuery(id+"F7.imprint","IMPRINT",EDGE,{"derivedFrom":sQuery(id+"F7.wireOp",EDGE,"E81.MirrorC")}),-1.0]])]});
            var Q1;
            Q1=makeQuery(id+"F7.imprint","IMPRINT",FACE,{"disambiguationData":[TD([[makeQuery(id+"F7.imprint","IMPRINT",EDGE,{"derivedFrom":sQuery(id+"F7.wireOp",EDGE,"E79")}),1.0]])]});
            var Q2;
            Q2=makeQuery(id+"F7.imprint","IMPRINT",FACE,{"disambiguationData":[TD([[makeQuery(id+"F7.imprint","IMPRINT",EDGE,{"derivedFrom":sQuery(id+"F7.wireOp",EDGE,"E80.MirrorC")}),-1.0]])]});
            var Q3;
            Q3=makeQuery(id+"F7.imprint","IMPRINT",FACE,{"disambiguationData":[TD([[makeQuery(id+"F7.imprint","IMPRINT",EDGE,{"derivedFrom":sQuery(id+"F7.wireOp",EDGE,"E82.MirrorC")}),1.0]])]});
            var Q4;
            {var subQ0=sQuery(id+"F7.wireOp",EDGE,"E100.right");var subQ1=sQuery(id+"F7.wireOp",EDGE,"E100.top");var subQ2=makeQuery(id+"F7.imprint","INTERSECT",VERTEX,{"derivedFrom":[subQ1,subQ0]});Q4=makeQuery(id+"F7.imprint","IMPRINT",FACE,{"disambiguationData":[TD([[makeQuery(id+"F7.imprint","IMPRINT",EDGE,{"disambiguationData":[TD([[subQ2,1.0]])],"derivedFrom":subQ1}),-1.0]])]});}
            var Q5;
            {var subQ0=sQuery(id+"F7.wireOp",EDGE,"E100.right");var subQ1=sQuery(id+"F7.wireOp",EDGE,"E100.top");var subQ2=makeQuery(id+"F7.imprint","INTERSECT",VERTEX,{"derivedFrom":[subQ1,subQ0]});Q5=makeQuery(id+"F7.imprint","IMPRINT",FACE,{"disambiguationData":[TD([[makeQuery(id+"F7.imprint","IMPRINT",EDGE,{"disambiguationData":[TD([[subQ2,1.0]])],"derivedFrom":subQ1}),1.0]])]});}
            var Q6;
            {var subQ0=sQuery(id+"F7.wireOp",EDGE,"E101.right");var subQ1=sQuery(id+"F7.wireOp",EDGE,"E101.top");var subQ2=makeQuery(id+"F7.imprint","INTERSECT",VERTEX,{"derivedFrom":[subQ1,subQ0]});Q6=makeQuery(id+"F7.imprint","IMPRINT",FACE,{"disambiguationData":[TD([[makeQuery(id+"F7.imprint","IMPRINT",EDGE,{"disambiguationData":[TD([[subQ2,1.0]])],"derivedFrom":subQ1}),1.0]])]});}
            var Q7;
            {var subQ0=sQuery(id+"F7.wireOp",EDGE,"E101.right");var subQ1=sQuery(id+"F7.wireOp",EDGE,"E101.top");var subQ2=makeQuery(id+"F7.imprint","INTERSECT",VERTEX,{"derivedFrom":[subQ1,subQ0]});Q7=makeQuery(id+"F7.imprint","IMPRINT",FACE,{"disambiguationData":[TD([[makeQuery(id+"F7.imprint","IMPRINT",EDGE,{"disambiguationData":[TD([[subQ2,1.0]])],"derivedFrom":subQ1}),-1.0]])]});}
            extrude(context, id + "F15", {"entities" : qUnion([Q0, Q1, Q2, Q3, Q4, Q5, Q6, Q7]), "operationType" : NewBodyOperationType.REMOVE, "oppositeDirection" : true, "depth" : 17.53 * mm, "offsetDistance" : 25.4 * mm});
        }
        {
            var Q0;
            Q0=makeQuery(id+"F8.imprint","IMPRINT",FACE,{"disambiguationData":[TD([[makeQuery(id+"F8.imprint","IMPRINT",EDGE,{"derivedFrom":sQuery(id+"F8.wireOp",EDGE,"E107.MirrorC")}),-1.0]])]});
            var Q1;
            Q1=makeQuery(id+"F8.imprint","IMPRINT",FACE,{"disambiguationData":[TD([[makeQuery(id+"F8.imprint","IMPRINT",EDGE,{"derivedFrom":sQuery(id+"F8.wireOp",EDGE,"E105")}),1.0]])]});
            var Q2;
            Q2=makeQuery(id+"F8.imprint","IMPRINT",FACE,{"disambiguationData":[TD([[makeQuery(id+"F8.imprint","IMPRINT",EDGE,{"derivedFrom":sQuery(id+"F8.wireOp",EDGE,"E106.MirrorC")}),-1.0]])]});
            var Q3;
            Q3=makeQuery(id+"F8.imprint","IMPRINT",FACE,{"disambiguationData":[TD([[makeQuery(id+"F8.imprint","IMPRINT",EDGE,{"derivedFrom":sQuery(id+"F8.wireOp",EDGE,"E108.MirrorC")}),1.0]])]});
            var Q4;
            {var subQ0=sQuery(id+"F8.wireOp",EDGE,"E126.right");var subQ1=sQuery(id+"F8.wireOp",EDGE,"E126.top");var subQ2=makeQuery(id+"F8.imprint","INTERSECT",VERTEX,{"derivedFrom":[subQ1,subQ0]});Q4=makeQuery(id+"F8.imprint","IMPRINT",FACE,{"disambiguationData":[TD([[makeQuery(id+"F8.imprint","IMPRINT",EDGE,{"disambiguationData":[TD([[subQ2,1.0]])],"derivedFrom":subQ1}),-1.0]])]});}
            var Q5;
            {var subQ0=sQuery(id+"F8.wireOp",EDGE,"E126.right");var subQ1=sQuery(id+"F8.wireOp",EDGE,"E126.top");var subQ2=makeQuery(id+"F8.imprint","INTERSECT",VERTEX,{"derivedFrom":[subQ1,subQ0]});Q5=makeQuery(id+"F8.imprint","IMPRINT",FACE,{"disambiguationData":[TD([[makeQuery(id+"F8.imprint","IMPRINT",EDGE,{"disambiguationData":[TD([[subQ2,1.0]])],"derivedFrom":subQ1}),1.0]])]});}
            var Q6;
            {var subQ0=sQuery(id+"F8.wireOp",EDGE,"E127.right");var subQ1=sQuery(id+"F8.wireOp",EDGE,"E127.top");var subQ2=makeQuery(id+"F8.imprint","INTERSECT",VERTEX,{"derivedFrom":[subQ1,subQ0]});Q6=makeQuery(id+"F8.imprint","IMPRINT",FACE,{"disambiguationData":[TD([[makeQuery(id+"F8.imprint","IMPRINT",EDGE,{"disambiguationData":[TD([[subQ2,1.0]])],"derivedFrom":subQ1}),1.0]])]});}
            var Q7;
            {var subQ0=sQuery(id+"F8.wireOp",EDGE,"E127.right");var subQ1=sQuery(id+"F8.wireOp",EDGE,"E127.top");var subQ2=makeQuery(id+"F8.imprint","INTERSECT",VERTEX,{"derivedFrom":[subQ1,subQ0]});Q7=makeQuery(id+"F8.imprint","IMPRINT",FACE,{"disambiguationData":[TD([[makeQuery(id+"F8.imprint","IMPRINT",EDGE,{"disambiguationData":[TD([[subQ2,1.0]])],"derivedFrom":subQ1}),-1.0]])]});}
            extrude(context, id + "F16", {"entities" : qUnion([Q0, Q1, Q2, Q3, Q4, Q5, Q6, Q7]), "operationType" : NewBodyOperationType.REMOVE, "oppositeDirection" : true, "depth" : 17.53 * mm, "offsetDistance" : 25.4 * mm});
        }
        {
            var Q0;
            Q0=makeQuery(id+"F2.imprint","IMPRINT",FACE,{"disambiguationData":[TD([[makeQuery(id+"F2.imprint","IMPRINT",EDGE,{"derivedFrom":sQuery(id+"F2.wireOp",EDGE,"E5.MirrorC")}),-1.0]])]});
            var Q1;
            Q1=makeQuery(id+"F2.imprint","IMPRINT",FACE,{"disambiguationData":[TD([[makeQuery(id+"F2.imprint","IMPRINT",EDGE,{"derivedFrom":sQuery(id+"F2.wireOp",EDGE,"E6.MirrorC")}),1.0]])]});
            var Q2;
            Q2=makeQuery(id+"F2.imprint","IMPRINT",FACE,{"disambiguationData":[TD([[makeQuery(id+"F2.imprint","IMPRINT",EDGE,{"derivedFrom":sQuery(id+"F2.wireOp",EDGE,"E4.MirrorC")}),-1.0]])]});
            var Q3;
            Q3=makeQuery(id+"F2.imprint","IMPRINT",FACE,{"disambiguationData":[TD([[makeQuery(id+"F2.imprint","IMPRINT",EDGE,{"derivedFrom":sQuery(id+"F2.wireOp",EDGE,"E3")}),1.0]])]});
            var Q4;
            Q4=sQuery(id+"F2.wireOp",EDGE,"E3");
            var Q5;
            Q5=sQuery(id+"F2.wireOp",EDGE,"E5.MirrorC");
            var Q6;
            Q6=sQuery(id+"F2.wireOp",EDGE,"E4.MirrorC");
            var Q7;
            Q7=sQuery(id+"F2.wireOp",EDGE,"E6.MirrorC");
            extrude(context, id + "F17", {"entities" : qUnion([Q0, Q1, Q2, Q3]), "operationType" : NewBodyOperationType.REMOVE, "surfaceEntities" : qUnion([Q4, Q5, Q6, Q7]), "oppositeDirection" : true, "depth" : 17.53 * mm, "offsetDistance" : 25.4 * mm});
        }
        {
            var Q0;
            Q0=makeQuery(id+"F7.imprint","IMPRINT",FACE,{"disambiguationData":[TD([[makeQuery(id+"F7.imprint","IMPRINT",EDGE,{"derivedFrom":sQuery(id+"F7.wireOp",EDGE,"E80.MirrorC")}),1.0]])]});
            var Q1;
            Q1=makeQuery(id+"F7.imprint","IMPRINT",FACE,{"disambiguationData":[TD([[makeQuery(id+"F7.imprint","IMPRINT",EDGE,{"derivedFrom":sQuery(id+"F7.wireOp",EDGE,"E82.MirrorC")}),-1.0]])]});
            var Q2;
            Q2=makeQuery(id+"F7.imprint","IMPRINT",FACE,{"disambiguationData":[TD([[makeQuery(id+"F7.imprint","IMPRINT",EDGE,{"derivedFrom":sQuery(id+"F7.wireOp",EDGE,"E81.MirrorC")}),1.0]])]});
            var Q3;
            Q3=makeQuery(id+"F7.imprint","IMPRINT",FACE,{"disambiguationData":[TD([[makeQuery(id+"F7.imprint","IMPRINT",EDGE,{"derivedFrom":sQuery(id+"F7.wireOp",EDGE,"E79")}),-1.0]])]});
            extrude(context, id + "F18", {"entities" : qUnion([Q0, Q1, Q2, Q3]), "operationType" : NewBodyOperationType.REMOVE, "oppositeDirection" : true, "depth" : 4.83 * mm, "offsetDistance" : 25.4 * mm});
        }
        {
            var Q0;
            Q0=makeQuery(id+"F8.imprint","IMPRINT",FACE,{"disambiguationData":[TD([[makeQuery(id+"F8.imprint","IMPRINT",EDGE,{"derivedFrom":sQuery(id+"F8.wireOp",EDGE,"E105")}),-1.0]])]});
            var Q1;
            Q1=makeQuery(id+"F8.imprint","IMPRINT",FACE,{"disambiguationData":[TD([[makeQuery(id+"F8.imprint","IMPRINT",EDGE,{"derivedFrom":sQuery(id+"F8.wireOp",EDGE,"E107.MirrorC")}),1.0]])]});
            var Q2;
            Q2=makeQuery(id+"F8.imprint","IMPRINT",FACE,{"disambiguationData":[TD([[makeQuery(id+"F8.imprint","IMPRINT",EDGE,{"derivedFrom":sQuery(id+"F8.wireOp",EDGE,"E108.MirrorC")}),-1.0]])]});
            var Q3;
            Q3=makeQuery(id+"F8.imprint","IMPRINT",FACE,{"disambiguationData":[TD([[makeQuery(id+"F8.imprint","IMPRINT",EDGE,{"derivedFrom":sQuery(id+"F8.wireOp",EDGE,"E106.MirrorC")}),1.0]])]});
            extrude(context, id + "F19", {"entities" : qUnion([Q0, Q1, Q2, Q3]), "operationType" : NewBodyOperationType.REMOVE, "oppositeDirection" : true, "depth" : 4.83 * mm, "offsetDistance" : 25.4 * mm});
        }
        {
            var Q0;
            Q0=makeQuery(id+"F5.imprint","IMPRINT",FACE,{"disambiguationData":[TD([[makeQuery(id+"F5.imprint","IMPRINT",EDGE,{"derivedFrom":sQuery(id+"F5.wireOp",EDGE,"E24")}),-1.0]])]});
            var Q1;
            Q1=makeQuery(id+"F5.imprint","IMPRINT",FACE,{"disambiguationData":[TD([[makeQuery(id+"F5.imprint","IMPRINT",EDGE,{"derivedFrom":sQuery(id+"F5.wireOp",EDGE,"E26.MirrorC")}),1.0]])]});
            var Q2;
            Q2=makeQuery(id+"F5.imprint","IMPRINT",FACE,{"disambiguationData":[TD([[makeQuery(id+"F5.imprint","IMPRINT",EDGE,{"derivedFrom":sQuery(id+"F5.wireOp",EDGE,"E27.MirrorC")}),-1.0]])]});
            var Q3;
            Q3=makeQuery(id+"F5.imprint","IMPRINT",FACE,{"disambiguationData":[TD([[makeQuery(id+"F5.imprint","IMPRINT",EDGE,{"derivedFrom":sQuery(id+"F5.wireOp",EDGE,"E25.MirrorC")}),1.0]])]});
            extrude(context, id + "F20", {"entities" : qUnion([Q0, Q1, Q2, Q3]), "operationType" : NewBodyOperationType.REMOVE, "oppositeDirection" : true, "depth" : 4.83 * mm, "offsetDistance" : 25.4 * mm});
        }
        {
            var Q0;
            Q0=makeQuery(id+"F6.imprint","IMPRINT",FACE,{"disambiguationData":[TD([[makeQuery(id+"F6.imprint","IMPRINT",EDGE,{"derivedFrom":sQuery(id+"F6.wireOp",EDGE,"E50")}),-1.0]])]});
            var Q1;
            Q1=makeQuery(id+"F6.imprint","IMPRINT",FACE,{"disambiguationData":[TD([[makeQuery(id+"F6.imprint","IMPRINT",EDGE,{"derivedFrom":sQuery(id+"F6.wireOp",EDGE,"E52.MirrorC")}),1.0]])]});
            var Q2;
            Q2=makeQuery(id+"F6.imprint","IMPRINT",FACE,{"disambiguationData":[TD([[makeQuery(id+"F6.imprint","IMPRINT",EDGE,{"derivedFrom":sQuery(id+"F6.wireOp",EDGE,"E53.MirrorC")}),-1.0]])]});
            var Q3;
            Q3=makeQuery(id+"F6.imprint","IMPRINT",FACE,{"disambiguationData":[TD([[makeQuery(id+"F6.imprint","IMPRINT",EDGE,{"derivedFrom":sQuery(id+"F6.wireOp",EDGE,"E51.MirrorC")}),1.0]])]});
            extrude(context, id + "F21", {"entities" : qUnion([Q0, Q1, Q2, Q3]), "operationType" : NewBodyOperationType.REMOVE, "oppositeDirection" : true, "depth" : 4.83 * mm, "offsetDistance" : 25.4 * mm});
        }
        {
            var Q0;
            {var subQ5=sQuery(id+"F5.wireOp",EDGE,"E37.MirrorCS");Q0=makeQuery(id+"F5.imprint","IMPRINT",FACE,{"disambiguationData":[TD([[makeQuery(id+"F5.imprint","IMPRINT",EDGE,{"derivedFrom":subQ5}),-1.0]])]});}
            extrude(context, id + "F22", {"entities" : qUnion([Q0]), "operationType" : NewBodyOperationType.REMOVE, "oppositeDirection" : true, "depth" : 11.18 * mm, "offsetDistance" : 25.4 * mm});
        }
        {
            var Q0;
            {var subQ5=sQuery(id+"F6.wireOp",EDGE,"E63.MirrorCS");Q0=makeQuery(id+"F6.imprint","IMPRINT",FACE,{"disambiguationData":[TD([[makeQuery(id+"F6.imprint","IMPRINT",EDGE,{"derivedFrom":subQ5}),-1.0]])]});}
            extrude(context, id + "F23", {"entities" : qUnion([Q0]), "operationType" : NewBodyOperationType.REMOVE, "oppositeDirection" : true, "depth" : 11.18 * mm, "offsetDistance" : 25.4 * mm});
        }
        {
            var Q0;
            {var subQ5=sQuery(id+"F7.wireOp",EDGE,"E92.MirrorCS");Q0=makeQuery(id+"F7.imprint","IMPRINT",FACE,{"disambiguationData":[TD([[makeQuery(id+"F7.imprint","IMPRINT",EDGE,{"derivedFrom":subQ5}),-1.0]])]});}
            extrude(context, id + "F24", {"entities" : qUnion([Q0]), "operationType" : NewBodyOperationType.REMOVE, "oppositeDirection" : true, "depth" : 11.18 * mm, "offsetDistance" : 25.4 * mm});
        }
        {
            var Q0;
            {var subQ5=sQuery(id+"F8.wireOp",EDGE,"E118.MirrorCS");Q0=makeQuery(id+"F8.imprint","IMPRINT",FACE,{"disambiguationData":[TD([[makeQuery(id+"F8.imprint","IMPRINT",EDGE,{"derivedFrom":subQ5}),-1.0]])]});}
            extrude(context, id + "F25", {"entities" : qUnion([Q0]), "operationType" : NewBodyOperationType.REMOVE, "oppositeDirection" : true, "depth" : 11.18 * mm, "offsetDistance" : 25.4 * mm});
        }
        {
            var Q0;
            {var subQ0=sQuery(id+"F2.wireOp",EDGE,"E18.MirrorCS");Q0=makeQuery(id+"F2.imprint","IMPRINT",FACE,{"disambiguationData":[TD([[makeQuery(id+"F2.imprint","IMPRINT",EDGE,{"derivedFrom":subQ0}),-1.0]])]});}
            var Q1;
            {var subQ5=sQuery(id+"F2.wireOp",EDGE,"E20.MirrorCS");Q1=makeQuery(id+"F2.imprint","IMPRINT",FACE,{"disambiguationData":[TD([[makeQuery(id+"F2.imprint","IMPRINT",EDGE,{"derivedFrom":subQ5}),-1.0]])]});}
            extrude(context, id + "F26", {"entities" : qUnion([Q0, Q1]), "operationType" : NewBodyOperationType.REMOVE, "oppositeDirection" : true, "depth" : 11.18 * mm, "offsetDistance" : 25.4 * mm});
        }
        {
            var Q0;
            Q0=makeQuery(id+"F1.opExtrude","CAP_FACE",FACE,{"disambiguationData":[OSD([sQuery(id+"F0.wireOp",EDGE,"E0.bottom"),sQuery(id+"F0.wireOp",EDGE,"E0.top"),sQuery(id+"F0.wireOp",EDGE,"E0.left"),sQuery(id+"F0.wireOp",EDGE,"E0.right")])],"isStart":true});
            var sketch = newSketch(context, id + "F27", { "sketchPlane" : qUnion([Q0])});
            skSolve(sketch);
        }
        {
            var Q0;
            Q0=makeQuery(id+"F27.imprint","IMPRINT",FACE,{"disambiguationData":[TD([[makeQuery(id+"F27.imprint","IMPRINT",EDGE,{"derivedFrom":makeQuery(id+"F1.opExtrude","CAP_EDGE",EDGE,{"disambiguationData":[OSD([sQuery(id+"F0.wireOp",EDGE,"E0.bottom")])],"isStart":true})}),1.0]])]});
            var sketch = newSketch(context, id + "F28", { "sketchPlane" : qUnion([Q0])});
            skLineSegment(sketch, "E130.bottom", {"start": v(-62.23, -62.23) * mm, "end": v(62.23, -62.23) * mm});
            skLineSegment(sketch, "E130.top", {"start": v(-62.23, 62.23) * mm, "end": v(62.23, 62.23) * mm});
            skLineSegment(sketch, "E130.left", {"start": v(-62.23, -62.23) * mm, "end": v(-62.23, 62.23) * mm});
            skLineSegment(sketch, "E130.right", {"start": v(62.23, -62.23) * mm, "end": v(62.23, 62.23) * mm});
            skPoint(sketch, "E130.middle", {"position": v(0, 0) * mm});
            skLineSegment(sketch, "E131.bottom", {"start": v(-62.23, -62.23) * mm, "end": v(-55.58, -62.23) * mm});
            skLineSegment(sketch, "E131.top", {"start": v(-62.23, -51.05) * mm, "end": v(-55.58, -51.05) * mm});
            skLineSegment(sketch, "E131.left", {"start": v(-62.23, -62.23) * mm, "end": v(-62.23, -51.05) * mm});
            skLineSegment(sketch, "E131.right", {"start": v(-55.58, -62.23) * mm, "end": v(-55.58, -51.05) * mm});
            skLineSegment(sketch, "E132.bottom", {"start": v(62.23, -62.23) * mm, "end": v(62.23, -55.58) * mm});
            skLineSegment(sketch, "E132.top", {"start": v(51.05, -62.23) * mm, "end": v(51.05, -55.58) * mm});
            skLineSegment(sketch, "E132.left", {"start": v(62.23, -62.23) * mm, "end": v(51.05, -62.23) * mm});
            skLineSegment(sketch, "E132.right", {"start": v(62.23, -55.58) * mm, "end": v(51.05, -55.58) * mm});
            skLineSegment(sketch, "E133.bottom", {"start": v(62.23, 62.23) * mm, "end": v(55.58, 62.23) * mm});
            skLineSegment(sketch, "E133.top", {"start": v(62.23, 51.05) * mm, "end": v(55.58, 51.05) * mm});
            skLineSegment(sketch, "E133.left", {"start": v(62.23, 62.23) * mm, "end": v(62.23, 51.05) * mm});
            skLineSegment(sketch, "E133.right", {"start": v(55.58, 62.23) * mm, "end": v(55.58, 51.05) * mm});
            skLineSegment(sketch, "E134.bottom", {"start": v(-62.23, 62.23) * mm, "end": v(-62.23, 55.58) * mm});
            skLineSegment(sketch, "E134.top", {"start": v(-51.05, 62.23) * mm, "end": v(-51.05, 55.58) * mm});
            skLineSegment(sketch, "E134.left", {"start": v(-62.23, 62.23) * mm, "end": v(-51.05, 62.23) * mm});
            skLineSegment(sketch, "E134.right", {"start": v(-62.23, 55.58) * mm, "end": v(-51.05, 55.58) * mm});
            skSolve(sketch);
        }
        {
            var Q0;
            {var subQ4=sQuery(id+"F28.wireOp",EDGE,"E133.top");Q0=makeQuery(id+"F28.imprint","IMPRINT",FACE,{"disambiguationData":[TD([[makeQuery(id+"F28.imprint","IMPRINT",EDGE,{"derivedFrom":subQ4}),-1.0]])]});}
            var Q1;
            {var subQ3=sQuery(id+"F28.wireOp",EDGE,"E134.top");Q1=makeQuery(id+"F28.imprint","IMPRINT",FACE,{"disambiguationData":[TD([[makeQuery(id+"F28.imprint","IMPRINT",EDGE,{"derivedFrom":subQ3}),-1.0]])]});}
            var Q2;
            {var subQ4=sQuery(id+"F28.wireOp",EDGE,"E131.top");Q2=makeQuery(id+"F28.imprint","IMPRINT",FACE,{"disambiguationData":[TD([[makeQuery(id+"F28.imprint","IMPRINT",EDGE,{"derivedFrom":subQ4}),-1.0]])]});}
            var Q3;
            {var subQ3=sQuery(id+"F28.wireOp",EDGE,"E132.top");Q3=makeQuery(id+"F28.imprint","IMPRINT",FACE,{"disambiguationData":[TD([[makeQuery(id+"F28.imprint","IMPRINT",EDGE,{"derivedFrom":subQ3}),-1.0]])]});}
            extrude(context, id + "F29", {"entities" : qUnion([Q0, Q1, Q2, Q3]), "operationType" : NewBodyOperationType.REMOVE, "oppositeDirection" : true, "depth" : 127 * mm, "offsetDistance" : 25.4 * mm});
        }
        {
            var Q0;
            Q0=makeQuery(id+"F4.boolean.opBoolean","COPY",EDGE,{"derivedFrom":makeQuery(id+"F4.opExtrude","SWEPT_EDGE",EDGE,{"disambiguationData":[OSD([sQuery(id+"F2.wireOp",EDGE,"E7.3"),sQuery(id+"F2.wireOp",EDGE,"E8.right")])]})});
            var Q1;
            Q1=makeQuery(id+"F4.boolean.opBoolean","COPY",EDGE,{"derivedFrom":makeQuery(id+"F4.opExtrude","SWEPT_EDGE",EDGE,{"disambiguationData":[OSD([sQuery(id+"F2.wireOp",EDGE,"E7.2"),sQuery(id+"F2.wireOp",EDGE,"E8.top")])]})});
            var Q2;
            Q2=makeQuery(id+"F4.boolean.opBoolean","COPY",EDGE,{"derivedFrom":makeQuery(id+"F4.opExtrude","SWEPT_EDGE",EDGE,{"disambiguationData":[OSD([sQuery(id+"F2.wireOp",EDGE,"E7.3"),sQuery(id+"F2.wireOp",EDGE,"E12.MirrorCS")])]})});
            var Q3;
            Q3=makeQuery(id+"F4.boolean.opBoolean","COPY",EDGE,{"derivedFrom":makeQuery(id+"F4.opExtrude","SWEPT_EDGE",EDGE,{"disambiguationData":[OSD([sQuery(id+"F2.wireOp",EDGE,"E7.0"),sQuery(id+"F2.wireOp",EDGE,"E11.MirrorCS")])]})});
            var Q4;
            Q4=makeQuery(id+"F4.boolean.opBoolean","COPY",EDGE,{"derivedFrom":makeQuery(id+"F4.opExtrude","SWEPT_EDGE",EDGE,{"disambiguationData":[OSD([sQuery(id+"F2.wireOp",EDGE,"E7.0"),sQuery(id+"F2.wireOp",EDGE,"E13.MirrorCS")])]})});
            var Q5;
            Q5=makeQuery(id+"F4.boolean.opBoolean","COPY",EDGE,{"derivedFrom":makeQuery(id+"F4.opExtrude","SWEPT_EDGE",EDGE,{"disambiguationData":[OSD([sQuery(id+"F2.wireOp",EDGE,"E7.1"),sQuery(id+"F2.wireOp",EDGE,"E14.MirrorCS")])]})});
            var Q6;
            Q6=makeQuery(id+"F4.boolean.opBoolean","COPY",EDGE,{"derivedFrom":makeQuery(id+"F4.opExtrude","SWEPT_EDGE",EDGE,{"disambiguationData":[OSD([sQuery(id+"F2.wireOp",EDGE,"E7.2"),sQuery(id+"F2.wireOp",EDGE,"E10.MirrorCS")])]})});
            var Q7;
            Q7=makeQuery(id+"F4.boolean.opBoolean","COPY",EDGE,{"derivedFrom":makeQuery(id+"F4.opExtrude","SWEPT_EDGE",EDGE,{"disambiguationData":[OSD([sQuery(id+"F2.wireOp",EDGE,"E7.1"),sQuery(id+"F2.wireOp",EDGE,"E9.MirrorCS")])]})});
            chamfer(context, id + "F30", {"entities" : qUnion([Q0, Q1, Q2, Q3, Q4, Q5, Q6, Q7]), "width" : 5.48 * mm, "tangentPropagation" : true});
        }
        {
            var Q0;
            Q0=makeQuery(id+"F21.boolean.opBoolean","COPY",EDGE,{"derivedFrom":makeQuery(id+"F21.opExtrude","SWEPT_EDGE",EDGE,{"disambiguationData":[OSD([sQuery(id+"F6.wireOp",EDGE,"E54.0"),sQuery(id+"F6.wireOp",EDGE,"E54.3")])]})});
            var Q1;
            Q1=makeQuery(id+"F21.boolean.opBoolean","COPY",EDGE,{"derivedFrom":makeQuery(id+"F21.opExtrude","SWEPT_EDGE",EDGE,{"disambiguationData":[OSD([sQuery(id+"F6.wireOp",EDGE,"E54.3"),sQuery(id+"F6.wireOp",EDGE,"E59.MirrorCS")])]})});
            var Q2;
            Q2=makeQuery(id+"F21.boolean.opBoolean","COPY",EDGE,{"derivedFrom":makeQuery(id+"F21.opExtrude","SWEPT_EDGE",EDGE,{"disambiguationData":[OSD([sQuery(id+"F6.wireOp",EDGE,"E54.0"),sQuery(id+"F6.wireOp",EDGE,"E54.1")])]})});
            var Q3;
            Q3=makeQuery(id+"F12.boolean.opBoolean","COPY",EDGE,{"derivedFrom":makeQuery(id+"F12.opExtrude","SWEPT_EDGE",EDGE,{"disambiguationData":[OSD([sQuery(id+"F6.wireOp",EDGE,"E54.1"),sQuery(id+"F6.wireOp",EDGE,"E61.MirrorCS")])]})});
            var Q4;
            Q4=makeQuery(id+"F12.boolean.opBoolean","COPY",EDGE,{"derivedFrom":makeQuery(id+"F12.opExtrude","SWEPT_EDGE",EDGE,{"disambiguationData":[OSD([sQuery(id+"F6.wireOp",EDGE,"E60.MirrorCS"),sQuery(id+"F6.wireOp",EDGE,"E61.MirrorCS")])]})});
            var Q5;
            Q5=makeQuery(id+"F12.boolean.opBoolean","COPY",EDGE,{"derivedFrom":makeQuery(id+"F12.opExtrude","SWEPT_EDGE",EDGE,{"disambiguationData":[OSD([sQuery(id+"F6.wireOp",EDGE,"E56.MirrorCS"),sQuery(id+"F6.wireOp",EDGE,"E57.MirrorCS")])]})});
            var Q6;
            Q6=makeQuery(id+"F21.boolean.opBoolean","COPY",EDGE,{"derivedFrom":makeQuery(id+"F21.opExtrude","SWEPT_EDGE",EDGE,{"disambiguationData":[OSD([sQuery(id+"F6.wireOp",EDGE,"E54.1"),sQuery(id+"F6.wireOp",EDGE,"E54.2")])]})});
            var Q7;
            Q7=makeQuery(id+"F12.boolean.opBoolean","COPY",EDGE,{"derivedFrom":makeQuery(id+"F12.opExtrude","SWEPT_EDGE",EDGE,{"disambiguationData":[OSD([sQuery(id+"F6.wireOp",EDGE,"E54.1"),sQuery(id+"F6.wireOp",EDGE,"E56.MirrorCS")])]})});
            var Q8;
            Q8=makeQuery(id+"F12.boolean.opBoolean","COPY",EDGE,{"derivedFrom":makeQuery(id+"F12.opExtrude","SWEPT_EDGE",EDGE,{"disambiguationData":[OSD([sQuery(id+"F6.wireOp",EDGE,"E54.2"),sQuery(id+"F6.wireOp",EDGE,"E55.top")])]})});
            var Q9;
            Q9=makeQuery(id+"F21.boolean.opBoolean","COPY",EDGE,{"derivedFrom":makeQuery(id+"F21.opExtrude","SWEPT_EDGE",EDGE,{"disambiguationData":[OSD([sQuery(id+"F6.wireOp",EDGE,"E54.2"),sQuery(id+"F6.wireOp",EDGE,"E54.3")])]})});
            var Q10;
            Q10=makeQuery(id+"F21.boolean.opBoolean","COPY",EDGE,{"derivedFrom":makeQuery(id+"F21.opExtrude","SWEPT_EDGE",EDGE,{"disambiguationData":[OSD([sQuery(id+"F6.wireOp",EDGE,"E54.3"),sQuery(id+"F6.wireOp",EDGE,"E55.right")])]})});
            var Q11;
            Q11=makeQuery(id+"F21.boolean.opBoolean","COPY",EDGE,{"derivedFrom":makeQuery(id+"F21.opExtrude","SWEPT_EDGE",EDGE,{"disambiguationData":[OSD([sQuery(id+"F6.wireOp",EDGE,"E55.top"),sQuery(id+"F6.wireOp",EDGE,"E55.right"),sQuery(id+"F6.wireOp",EDGE,"E73")])]})});
            var Q12;
            Q12=makeQuery(id+"F21.boolean.opBoolean","COPY",EDGE,{"derivedFrom":makeQuery(id+"F21.opExtrude","SWEPT_EDGE",EDGE,{"disambiguationData":[OSD([sQuery(id+"F6.wireOp",EDGE,"E58.MirrorCS"),sQuery(id+"F6.wireOp",EDGE,"E59.MirrorCS"),sQuery(id+"F6.wireOp",EDGE,"E73")])]})});
            var Q13;
            Q13=makeQuery(id+"F9.boolean.opBoolean","COPY",EDGE,{"derivedFrom":makeQuery(id+"F9.opExtrude","SWEPT_EDGE",EDGE,{"disambiguationData":[OSD([sQuery(id+"F5.wireOp",EDGE,"E28.2"),sQuery(id+"F5.wireOp",EDGE,"E29.top")])]})});
            var Q14;
            Q14=makeQuery(id+"F20.boolean.opBoolean","COPY",EDGE,{"derivedFrom":makeQuery(id+"F20.opExtrude","SWEPT_EDGE",EDGE,{"disambiguationData":[OSD([sQuery(id+"F5.wireOp",EDGE,"E28.2"),sQuery(id+"F5.wireOp",EDGE,"E28.3")])]})});
            var Q15;
            Q15=makeQuery(id+"F20.boolean.opBoolean","COPY",EDGE,{"derivedFrom":makeQuery(id+"F20.opExtrude","SWEPT_EDGE",EDGE,{"disambiguationData":[OSD([sQuery(id+"F5.wireOp",EDGE,"E28.3"),sQuery(id+"F5.wireOp",EDGE,"E29.right")])]})});
            var Q16;
            Q16=makeQuery(id+"F20.boolean.opBoolean","COPY",EDGE,{"derivedFrom":makeQuery(id+"F20.opExtrude","SWEPT_EDGE",EDGE,{"disambiguationData":[OSD([sQuery(id+"F5.wireOp",EDGE,"E29.top"),sQuery(id+"F5.wireOp",EDGE,"E29.right"),sQuery(id+"F5.wireOp",EDGE,"E44")])]})});
            var Q17;
            Q17=makeQuery(id+"F20.boolean.opBoolean","COPY",EDGE,{"derivedFrom":makeQuery(id+"F20.opExtrude","SWEPT_EDGE",EDGE,{"disambiguationData":[OSD([sQuery(id+"F5.wireOp",EDGE,"E32.MirrorCS"),sQuery(id+"F5.wireOp",EDGE,"E33.MirrorCS"),sQuery(id+"F5.wireOp",EDGE,"E44")])]})});
            var Q18;
            Q18=makeQuery(id+"F20.boolean.opBoolean","COPY",EDGE,{"derivedFrom":makeQuery(id+"F20.opExtrude","SWEPT_EDGE",EDGE,{"disambiguationData":[OSD([sQuery(id+"F5.wireOp",EDGE,"E28.3"),sQuery(id+"F5.wireOp",EDGE,"E33.MirrorCS")])]})});
            var Q19;
            Q19=makeQuery(id+"F20.boolean.opBoolean","COPY",EDGE,{"derivedFrom":makeQuery(id+"F20.opExtrude","SWEPT_EDGE",EDGE,{"disambiguationData":[OSD([sQuery(id+"F5.wireOp",EDGE,"E28.0"),sQuery(id+"F5.wireOp",EDGE,"E28.3")])]})});
            var Q20;
            Q20=makeQuery(id+"F19.boolean.opBoolean","COPY",EDGE,{"derivedFrom":makeQuery(id+"F19.opExtrude","SWEPT_EDGE",EDGE,{"disambiguationData":[OSD([sQuery(id+"F8.wireOp",EDGE,"E109.3"),sQuery(id+"F8.wireOp",EDGE,"E110.right")])]})});
            var Q21;
            Q21=makeQuery(id+"F19.boolean.opBoolean","COPY",EDGE,{"derivedFrom":makeQuery(id+"F19.opExtrude","SWEPT_EDGE",EDGE,{"disambiguationData":[OSD([sQuery(id+"F8.wireOp",EDGE,"E110.top"),sQuery(id+"F8.wireOp",EDGE,"E110.right"),sQuery(id+"F8.wireOp",EDGE,"E125")])]})});
            var Q22;
            Q22=makeQuery(id+"F19.boolean.opBoolean","COPY",EDGE,{"derivedFrom":makeQuery(id+"F19.opExtrude","SWEPT_EDGE",EDGE,{"disambiguationData":[OSD([sQuery(id+"F8.wireOp",EDGE,"E109.2"),sQuery(id+"F8.wireOp",EDGE,"E109.3")])]})});
            var Q23;
            Q23=makeQuery(id+"F19.boolean.opBoolean","COPY",EDGE,{"derivedFrom":makeQuery(id+"F19.opExtrude","SWEPT_EDGE",EDGE,{"disambiguationData":[OSD([sQuery(id+"F8.wireOp",EDGE,"E109.0"),sQuery(id+"F8.wireOp",EDGE,"E109.3")])]})});
            var Q24;
            Q24=makeQuery(id+"F19.boolean.opBoolean","COPY",EDGE,{"derivedFrom":makeQuery(id+"F19.opExtrude","SWEPT_EDGE",EDGE,{"disambiguationData":[OSD([sQuery(id+"F8.wireOp",EDGE,"E113.MirrorCS"),sQuery(id+"F8.wireOp",EDGE,"E114.MirrorCS"),sQuery(id+"F8.wireOp",EDGE,"E125")])]})});
            var Q25;
            Q25=makeQuery(id+"F19.boolean.opBoolean","COPY",EDGE,{"derivedFrom":makeQuery(id+"F19.opExtrude","SWEPT_EDGE",EDGE,{"disambiguationData":[OSD([sQuery(id+"F8.wireOp",EDGE,"E109.3"),sQuery(id+"F8.wireOp",EDGE,"E114.MirrorCS")])]})});
            var Q26;
            Q26=makeQuery(id+"F18.boolean.opBoolean","COPY",EDGE,{"derivedFrom":makeQuery(id+"F18.opExtrude","SWEPT_EDGE",EDGE,{"disambiguationData":[OSD([sQuery(id+"F7.wireOp",EDGE,"E83.2"),sQuery(id+"F7.wireOp",EDGE,"E83.3")])]})});
            var Q27;
            Q27=makeQuery(id+"F18.boolean.opBoolean","COPY",EDGE,{"derivedFrom":makeQuery(id+"F18.opExtrude","SWEPT_EDGE",EDGE,{"disambiguationData":[OSD([sQuery(id+"F7.wireOp",EDGE,"E83.3"),sQuery(id+"F7.wireOp",EDGE,"E84.right")])]})});
            var Q28;
            Q28=makeQuery(id+"F18.boolean.opBoolean","COPY",EDGE,{"derivedFrom":makeQuery(id+"F18.opExtrude","SWEPT_EDGE",EDGE,{"disambiguationData":[OSD([sQuery(id+"F7.wireOp",EDGE,"E84.top"),sQuery(id+"F7.wireOp",EDGE,"E84.right"),sQuery(id+"F7.wireOp",EDGE,"E99")])]})});
            var Q29;
            Q29=makeQuery(id+"F18.boolean.opBoolean","COPY",EDGE,{"derivedFrom":makeQuery(id+"F18.opExtrude","SWEPT_EDGE",EDGE,{"disambiguationData":[OSD([sQuery(id+"F7.wireOp",EDGE,"E83.0"),sQuery(id+"F7.wireOp",EDGE,"E83.3")])]})});
            var Q30;
            Q30=makeQuery(id+"F18.boolean.opBoolean","COPY",EDGE,{"derivedFrom":makeQuery(id+"F18.opExtrude","SWEPT_EDGE",EDGE,{"disambiguationData":[OSD([sQuery(id+"F7.wireOp",EDGE,"E83.3"),sQuery(id+"F7.wireOp",EDGE,"E88.MirrorCS")])]})});
            var Q31;
            Q31=makeQuery(id+"F18.boolean.opBoolean","COPY",EDGE,{"derivedFrom":makeQuery(id+"F18.opExtrude","SWEPT_EDGE",EDGE,{"disambiguationData":[OSD([sQuery(id+"F7.wireOp",EDGE,"E87.MirrorCS"),sQuery(id+"F7.wireOp",EDGE,"E88.MirrorCS"),sQuery(id+"F7.wireOp",EDGE,"E99")])]})});
            var Q32;
            Q32=makeQuery(id+"F18.boolean.opBoolean","COPY",EDGE,{"derivedFrom":makeQuery(id+"F18.opExtrude","SWEPT_EDGE",EDGE,{"disambiguationData":[OSD([sQuery(id+"F7.wireOp",EDGE,"E83.0"),sQuery(id+"F7.wireOp",EDGE,"E83.1")])]})});
            var Q33;
            Q33=makeQuery(id+"F12.boolean.opBoolean","INTERSECT",EDGE,{"derivedFrom":[makeQuery(id+"F11.boolean.opBoolean","COPY",FACE,{"derivedFrom":makeQuery(id+"F11.opExtrude","SWEPT_FACE",FACE,{"disambiguationData":[OSD([sQuery(id+"F7.wireOp",EDGE,"E90.MirrorCS")])]})}),makeQuery(id+"F12.opExtrude","SWEPT_FACE",FACE,{"disambiguationData":[OSD([sQuery(id+"F6.wireOp",EDGE,"E56.MirrorCS")])]})]});
            var Q34;
            Q34=makeQuery(id+"F11.boolean.opBoolean","COPY",EDGE,{"derivedFrom":makeQuery(id+"F11.opExtrude","SWEPT_EDGE",EDGE,{"disambiguationData":[OSD([sQuery(id+"F7.wireOp",EDGE,"E83.2"),sQuery(id+"F7.wireOp",EDGE,"E86.MirrorCS")])]})});
            var Q35;
            Q35=makeQuery(id+"F11.boolean.opBoolean","COPY",EDGE,{"derivedFrom":makeQuery(id+"F11.opExtrude","SWEPT_EDGE",EDGE,{"disambiguationData":[OSD([sQuery(id+"F7.wireOp",EDGE,"E85.MirrorCS"),sQuery(id+"F7.wireOp",EDGE,"E86.MirrorCS")])]})});
            var Q36;
            Q36=makeQuery(id+"F11.boolean.opBoolean","COPY",EDGE,{"derivedFrom":makeQuery(id+"F11.opExtrude","SWEPT_EDGE",EDGE,{"disambiguationData":[OSD([sQuery(id+"F7.wireOp",EDGE,"E83.1"),sQuery(id+"F7.wireOp",EDGE,"E85.MirrorCS")])]})});
            var Q37;
            Q37=makeQuery(id+"F18.boolean.opBoolean","COPY",EDGE,{"derivedFrom":makeQuery(id+"F18.opExtrude","SWEPT_EDGE",EDGE,{"disambiguationData":[OSD([sQuery(id+"F7.wireOp",EDGE,"E83.1"),sQuery(id+"F7.wireOp",EDGE,"E83.2")])]})});
            var Q38;
            Q38=makeQuery(id+"F12.boolean.opBoolean","COPY",EDGE,{"derivedFrom":makeQuery(id+"F12.opExtrude","SWEPT_EDGE",EDGE,{"disambiguationData":[OSD([sQuery(id+"F6.wireOp",EDGE,"E54.2"),sQuery(id+"F6.wireOp",EDGE,"E57.MirrorCS")])]})});
            var Q39;
            Q39=makeQuery(id+"F11.boolean.opBoolean","COPY",EDGE,{"derivedFrom":makeQuery(id+"F11.opExtrude","SWEPT_EDGE",EDGE,{"disambiguationData":[OSD([sQuery(id+"F7.wireOp",EDGE,"E89.MirrorCS"),sQuery(id+"F7.wireOp",EDGE,"E90.MirrorCS")])]})});
            var Q40;
            Q40=makeQuery(id+"F9.boolean.opBoolean","COPY",EDGE,{"derivedFrom":makeQuery(id+"F9.opExtrude","SWEPT_EDGE",EDGE,{"disambiguationData":[OSD([sQuery(id+"F5.wireOp",EDGE,"E30.MirrorCS"),sQuery(id+"F5.wireOp",EDGE,"E31.MirrorCS")])]})});
            var Q41;
            Q41=makeQuery(id+"F9.boolean.opBoolean","COPY",EDGE,{"derivedFrom":makeQuery(id+"F9.opExtrude","SWEPT_EDGE",EDGE,{"disambiguationData":[OSD([sQuery(id+"F5.wireOp",EDGE,"E28.2"),sQuery(id+"F5.wireOp",EDGE,"E31.MirrorCS")])]})});
            var Q42;
            Q42=makeQuery(id+"F9.boolean.opBoolean","COPY",EDGE,{"derivedFrom":makeQuery(id+"F9.opExtrude","SWEPT_EDGE",EDGE,{"disambiguationData":[OSD([sQuery(id+"F5.wireOp",EDGE,"E28.1"),sQuery(id+"F5.wireOp",EDGE,"E30.MirrorCS")])]})});
            var Q43;
            Q43=makeQuery(id+"F20.boolean.opBoolean","COPY",EDGE,{"derivedFrom":makeQuery(id+"F20.opExtrude","SWEPT_EDGE",EDGE,{"disambiguationData":[OSD([sQuery(id+"F5.wireOp",EDGE,"E28.1"),sQuery(id+"F5.wireOp",EDGE,"E28.2")])]})});
            var Q44;
            Q44=makeQuery(id+"F20.boolean.opBoolean","COPY",EDGE,{"derivedFrom":makeQuery(id+"F20.opExtrude","SWEPT_EDGE",EDGE,{"disambiguationData":[OSD([sQuery(id+"F5.wireOp",EDGE,"E28.0"),sQuery(id+"F5.wireOp",EDGE,"E28.1")])]})});
            var Q45;
            Q45=makeQuery(id+"F9.boolean.opBoolean","COPY",EDGE,{"derivedFrom":makeQuery(id+"F9.opExtrude","SWEPT_EDGE",EDGE,{"disambiguationData":[OSD([sQuery(id+"F5.wireOp",EDGE,"E28.1"),sQuery(id+"F5.wireOp",EDGE,"E35.MirrorCS")])]})});
            var Q46;
            Q46=makeQuery(id+"F9.boolean.opBoolean","COPY",EDGE,{"derivedFrom":makeQuery(id+"F9.opExtrude","SWEPT_EDGE",EDGE,{"disambiguationData":[OSD([sQuery(id+"F5.wireOp",EDGE,"E34.MirrorCS"),sQuery(id+"F5.wireOp",EDGE,"E35.MirrorCS")])]})});
            var Q47;
            Q47=makeQuery(id+"F10.boolean.opBoolean","COPY",EDGE,{"derivedFrom":makeQuery(id+"F10.opExtrude","SWEPT_EDGE",EDGE,{"disambiguationData":[OSD([sQuery(id+"F8.wireOp",EDGE,"E111.MirrorCS"),sQuery(id+"F8.wireOp",EDGE,"E112.MirrorCS")])]})});
            var Q48;
            Q48=makeQuery(id+"F10.boolean.opBoolean","COPY",EDGE,{"derivedFrom":makeQuery(id+"F10.opExtrude","SWEPT_EDGE",EDGE,{"disambiguationData":[OSD([sQuery(id+"F8.wireOp",EDGE,"E109.1"),sQuery(id+"F8.wireOp",EDGE,"E111.MirrorCS")])]})});
            var Q49;
            Q49=makeQuery(id+"F10.boolean.opBoolean","COPY",EDGE,{"derivedFrom":makeQuery(id+"F10.opExtrude","SWEPT_EDGE",EDGE,{"disambiguationData":[OSD([sQuery(id+"F8.wireOp",EDGE,"E109.2"),sQuery(id+"F8.wireOp",EDGE,"E112.MirrorCS")])]})});
            var Q50;
            Q50=makeQuery(id+"F19.boolean.opBoolean","COPY",EDGE,{"derivedFrom":makeQuery(id+"F19.opExtrude","SWEPT_EDGE",EDGE,{"disambiguationData":[OSD([sQuery(id+"F8.wireOp",EDGE,"E109.1"),sQuery(id+"F8.wireOp",EDGE,"E109.2")])]})});
            var Q51;
            Q51=makeQuery(id+"F19.boolean.opBoolean","COPY",EDGE,{"derivedFrom":makeQuery(id+"F19.opExtrude","SWEPT_EDGE",EDGE,{"disambiguationData":[OSD([sQuery(id+"F8.wireOp",EDGE,"E109.0"),sQuery(id+"F8.wireOp",EDGE,"E109.1")])]})});
            var Q52;
            Q52=makeQuery(id+"F10.boolean.opBoolean","COPY",EDGE,{"derivedFrom":makeQuery(id+"F10.opExtrude","SWEPT_EDGE",EDGE,{"disambiguationData":[OSD([sQuery(id+"F8.wireOp",EDGE,"E115.MirrorCS"),sQuery(id+"F8.wireOp",EDGE,"E116.MirrorCS")])]})});
            var Q53;
            Q53=makeQuery(id+"F10.boolean.opBoolean","COPY",EDGE,{"derivedFrom":makeQuery(id+"F10.opExtrude","SWEPT_EDGE",EDGE,{"disambiguationData":[OSD([sQuery(id+"F8.wireOp",EDGE,"E109.1"),sQuery(id+"F8.wireOp",EDGE,"E116.MirrorCS")])]})});
            var Q54;
            Q54=makeQuery(id+"F3.boolean.opBoolean","COPY",EDGE,{"derivedFrom":makeQuery(id+"F3.opExtrude","SWEPT_EDGE",EDGE,{"disambiguationData":[OSD([sQuery(id+"F2.wireOp",EDGE,"E7.0"),sQuery(id+"F2.wireOp",EDGE,"E7.1")])]})});
            var Q55;
            Q55=makeQuery(id+"F3.boolean.opBoolean","COPY",EDGE,{"derivedFrom":makeQuery(id+"F3.opExtrude","SWEPT_EDGE",EDGE,{"disambiguationData":[OSD([sQuery(id+"F2.wireOp",EDGE,"E7.1"),sQuery(id+"F2.wireOp",EDGE,"E7.2")])]})});
            var Q56;
            Q56=makeQuery(id+"F3.boolean.opBoolean","COPY",EDGE,{"derivedFrom":makeQuery(id+"F3.opExtrude","SWEPT_EDGE",EDGE,{"disambiguationData":[OSD([sQuery(id+"F2.wireOp",EDGE,"E7.2"),sQuery(id+"F2.wireOp",EDGE,"E7.3")])]})});
            var Q57;
            Q57=makeQuery(id+"F3.boolean.opBoolean","COPY",EDGE,{"derivedFrom":makeQuery(id+"F3.opExtrude","SWEPT_EDGE",EDGE,{"disambiguationData":[OSD([sQuery(id+"F2.wireOp",EDGE,"E7.0"),sQuery(id+"F2.wireOp",EDGE,"E7.3")])]})});
            var Q58;
            Q58=makeQuery(id+"F12.boolean.opBoolean","COPY",EDGE,{"derivedFrom":makeQuery(id+"F12.opExtrude","SWEPT_EDGE",EDGE,{"disambiguationData":[OSD([sQuery(id+"F6.wireOp",EDGE,"E54.0"),sQuery(id+"F6.wireOp",EDGE,"E60.MirrorCS")])]})});
            var Q59;
            Q59=makeQuery(id+"F11.boolean.opBoolean","COPY",EDGE,{"derivedFrom":makeQuery(id+"F11.opExtrude","SWEPT_EDGE",EDGE,{"disambiguationData":[OSD([sQuery(id+"F7.wireOp",EDGE,"E83.0"),sQuery(id+"F7.wireOp",EDGE,"E89.MirrorCS")])]})});
            var Q60;
            Q60=makeQuery(id+"F10.boolean.opBoolean","COPY",EDGE,{"derivedFrom":makeQuery(id+"F10.opExtrude","SWEPT_EDGE",EDGE,{"disambiguationData":[OSD([sQuery(id+"F8.wireOp",EDGE,"E109.0"),sQuery(id+"F8.wireOp",EDGE,"E115.MirrorCS")])]})});
            var Q61;
            Q61=makeQuery(id+"F9.boolean.opBoolean","COPY",EDGE,{"derivedFrom":makeQuery(id+"F9.opExtrude","SWEPT_EDGE",EDGE,{"disambiguationData":[OSD([sQuery(id+"F5.wireOp",EDGE,"E28.0"),sQuery(id+"F5.wireOp",EDGE,"E34.MirrorCS")])]})});
            var Q62;
            Q62=makeQuery(id+"F11.boolean.opBoolean","INTERSECT",EDGE,{"derivedFrom":[makeQuery(id+"F10.boolean.opBoolean","COPY",FACE,{"derivedFrom":makeQuery(id+"F10.opExtrude","SWEPT_FACE",FACE,{"disambiguationData":[OSD([sQuery(id+"F8.wireOp",EDGE,"E116.MirrorCS")])]})}),makeQuery(id+"F11.opExtrude","SWEPT_FACE",FACE,{"disambiguationData":[OSD([sQuery(id+"F7.wireOp",EDGE,"E85.MirrorCS")])]})]});
            var Q63;
            Q63=makeQuery(id+"F10.boolean.opBoolean","INTERSECT",EDGE,{"derivedFrom":[makeQuery(id+"F9.boolean.opBoolean","COPY",FACE,{"derivedFrom":makeQuery(id+"F9.opExtrude","SWEPT_FACE",FACE,{"disambiguationData":[OSD([sQuery(id+"F5.wireOp",EDGE,"E35.MirrorCS")])]})}),makeQuery(id+"F10.opExtrude","SWEPT_FACE",FACE,{"disambiguationData":[OSD([sQuery(id+"F8.wireOp",EDGE,"E111.MirrorCS")])]})]});
            var Q64;
            Q64=makeQuery(id+"F12.boolean.opBoolean","INTERSECT",EDGE,{"derivedFrom":[makeQuery(id+"F9.boolean.opBoolean","COPY",FACE,{"derivedFrom":makeQuery(id+"F9.opExtrude","SWEPT_FACE",FACE,{"disambiguationData":[OSD([sQuery(id+"F5.wireOp",EDGE,"E30.MirrorCS")])]})}),makeQuery(id+"F12.opExtrude","SWEPT_FACE",FACE,{"disambiguationData":[OSD([sQuery(id+"F6.wireOp",EDGE,"E61.MirrorCS")])]})]});
            var Q65;
            Q65=makeQuery(id+"F11.boolean.opBoolean","COPY",EDGE,{"derivedFrom":makeQuery(id+"F11.opExtrude","CAP_EDGE",EDGE,{"disambiguationData":[OSD([sQuery(id+"F7.wireOp",EDGE,"E84.top"),sQuery(id+"F7.wireOp",EDGE,"E87.MirrorCS"),sQuery(id+"F7.wireOp",EDGE,"E99")])],"isStart":true})});
            var Q66;
            Q66=makeQuery(id+"F10.boolean.opBoolean","COPY",EDGE,{"derivedFrom":makeQuery(id+"F10.opExtrude","CAP_EDGE",EDGE,{"disambiguationData":[OSD([sQuery(id+"F8.wireOp",EDGE,"E110.top"),sQuery(id+"F8.wireOp",EDGE,"E113.MirrorCS"),sQuery(id+"F8.wireOp",EDGE,"E125")])],"isStart":true})});
            var Q67;
            Q67=makeQuery(id+"F12.boolean.opBoolean","COPY",EDGE,{"derivedFrom":makeQuery(id+"F12.opExtrude","CAP_EDGE",EDGE,{"disambiguationData":[OSD([sQuery(id+"F6.wireOp",EDGE,"E55.top"),sQuery(id+"F6.wireOp",EDGE,"E58.MirrorCS"),sQuery(id+"F6.wireOp",EDGE,"E73")])],"isStart":true})});
            var Q68;
            Q68=makeQuery(id+"F9.boolean.opBoolean","COPY",EDGE,{"derivedFrom":makeQuery(id+"F9.opExtrude","CAP_EDGE",EDGE,{"disambiguationData":[OSD([sQuery(id+"F5.wireOp",EDGE,"E29.top"),sQuery(id+"F5.wireOp",EDGE,"E32.MirrorCS"),sQuery(id+"F5.wireOp",EDGE,"E44")])],"isStart":true})});
            var Q69;
            Q69=makeQuery(id+"F11.boolean.opBoolean","COPY",EDGE,{"derivedFrom":makeQuery(id+"F11.opExtrude","SWEPT_EDGE",EDGE,{"disambiguationData":[OSD([sQuery(id+"F7.wireOp",EDGE,"E83.2"),sQuery(id+"F7.wireOp",EDGE,"E84.top")])]})});
            var Q70;
            Q70=makeQuery(id+"F18.boolean.opBoolean","COPY",EDGE,{"derivedFrom":makeQuery(id+"F18.opExtrude","CAP_EDGE",EDGE,{"disambiguationData":[OSD([sQuery(id+"F7.wireOp",EDGE,"E84.top")])],"isStart":false})});
            var Q71;
            Q71=makeQuery(id+"F10.boolean.opBoolean","COPY",EDGE,{"derivedFrom":makeQuery(id+"F10.opExtrude","SWEPT_EDGE",EDGE,{"disambiguationData":[OSD([sQuery(id+"F8.wireOp",EDGE,"E109.0"),sQuery(id+"F8.wireOp",EDGE,"E113.MirrorCS")])]})});
            var Q72;
            Q72=makeQuery(id+"F19.boolean.opBoolean","COPY",EDGE,{"derivedFrom":makeQuery(id+"F19.opExtrude","CAP_EDGE",EDGE,{"disambiguationData":[OSD([sQuery(id+"F8.wireOp",EDGE,"E113.MirrorCS")])],"isStart":false})});
            var Q73;
            Q73=makeQuery(id+"F9.boolean.opBoolean","COPY",EDGE,{"derivedFrom":makeQuery(id+"F9.opExtrude","SWEPT_EDGE",EDGE,{"disambiguationData":[OSD([sQuery(id+"F5.wireOp",EDGE,"E28.0"),sQuery(id+"F5.wireOp",EDGE,"E32.MirrorCS")])]})});
            var Q74;
            Q74=makeQuery(id+"F10.boolean.opBoolean","COPY",EDGE,{"derivedFrom":makeQuery(id+"F10.opExtrude","SWEPT_EDGE",EDGE,{"disambiguationData":[OSD([sQuery(id+"F8.wireOp",EDGE,"E109.2"),sQuery(id+"F8.wireOp",EDGE,"E110.top")])]})});
            var Q75;
            Q75=makeQuery(id+"F19.boolean.opBoolean","COPY",EDGE,{"derivedFrom":makeQuery(id+"F19.opExtrude","CAP_EDGE",EDGE,{"disambiguationData":[OSD([sQuery(id+"F8.wireOp",EDGE,"E110.top")])],"isStart":false})});
            var Q76;
            Q76=makeQuery(id+"F20.boolean.opBoolean","COPY",EDGE,{"derivedFrom":makeQuery(id+"F20.opExtrude","CAP_EDGE",EDGE,{"disambiguationData":[OSD([sQuery(id+"F5.wireOp",EDGE,"E32.MirrorCS")])],"isStart":false})});
            var Q77;
            Q77=makeQuery(id+"F20.boolean.opBoolean","COPY",EDGE,{"derivedFrom":makeQuery(id+"F20.opExtrude","CAP_EDGE",EDGE,{"disambiguationData":[OSD([sQuery(id+"F5.wireOp",EDGE,"E29.top")])],"isStart":false})});
            var Q78;
            Q78=makeQuery(id+"F12.boolean.opBoolean","COPY",EDGE,{"derivedFrom":makeQuery(id+"F12.opExtrude","SWEPT_EDGE",EDGE,{"disambiguationData":[OSD([sQuery(id+"F6.wireOp",EDGE,"E54.0"),sQuery(id+"F6.wireOp",EDGE,"E58.MirrorCS")])]})});
            var Q79;
            Q79=makeQuery(id+"F21.boolean.opBoolean","COPY",EDGE,{"derivedFrom":makeQuery(id+"F21.opExtrude","CAP_EDGE",EDGE,{"disambiguationData":[OSD([sQuery(id+"F6.wireOp",EDGE,"E58.MirrorCS")])],"isStart":false})});
            var Q80;
            Q80=makeQuery(id+"F18.boolean.opBoolean","COPY",EDGE,{"derivedFrom":makeQuery(id+"F18.opExtrude","CAP_EDGE",EDGE,{"disambiguationData":[OSD([sQuery(id+"F7.wireOp",EDGE,"E87.MirrorCS")])],"isStart":false})});
            var Q81;
            Q81=makeQuery(id+"F11.boolean.opBoolean","COPY",EDGE,{"derivedFrom":makeQuery(id+"F11.opExtrude","SWEPT_EDGE",EDGE,{"disambiguationData":[OSD([sQuery(id+"F7.wireOp",EDGE,"E83.0"),sQuery(id+"F7.wireOp",EDGE,"E87.MirrorCS")])]})});
            var Q82;
            Q82=makeQuery(id+"F21.boolean.opBoolean","COPY",EDGE,{"derivedFrom":makeQuery(id+"F21.opExtrude","CAP_EDGE",EDGE,{"disambiguationData":[OSD([sQuery(id+"F6.wireOp",EDGE,"E55.top")])],"isStart":false})});
            fillet(context, id + "F31", {"entities" : qUnion([Q0, Q1, Q2, Q3, Q4, Q5, Q6, Q7, Q8, Q9, Q10, Q11, Q12, Q13, Q14, Q15, Q16, Q17, Q18, Q19, Q20, Q21, Q22, Q23, Q24, Q25, Q26, Q27, Q28, Q29, Q30, Q31, Q32, Q33, Q34, Q35, Q36, Q37, Q38, Q39, Q40, Q41, Q42, Q43, Q44, Q45, Q46, Q47, Q48, Q49, Q50, Q51, Q52, Q53, Q54, Q55, Q56, Q57, Q58, Q59, Q60, Q61, Q62, Q63, Q64, Q65, Q66, Q67, Q68, Q69, Q70, Q71, Q72, Q73, Q74, Q75, Q76, Q77, Q78, Q79, Q80, Q81, Q82]), "radius" : 0.8 * mm, "tangentPropagation" : true, "allowEdgeOverflow" : false});
        }
        {
            var Q0;
            Q0=makeQuery(id+"F1.opExtrude","CAP_EDGE",EDGE,{"disambiguationData":[OSD([sQuery(id+"F0.wireOp",EDGE,"E0.top")])],"isStart":false});
            var Q1;
            Q1=makeQuery(id+"F1.opExtrude","CAP_EDGE",EDGE,{"disambiguationData":[OSD([sQuery(id+"F0.wireOp",EDGE,"E0.right")])],"isStart":false});
            var Q2;
            Q2=makeQuery(id+"F1.opExtrude","CAP_EDGE",EDGE,{"disambiguationData":[OSD([sQuery(id+"F0.wireOp",EDGE,"E0.bottom")])],"isStart":false});
            var Q3;
            Q3=makeQuery(id+"F1.opExtrude","CAP_EDGE",EDGE,{"disambiguationData":[OSD([sQuery(id+"F0.wireOp",EDGE,"E0.left")])],"isStart":false});
            var Q4;
            Q4=makeQuery(id+"F1.opExtrude","SWEPT_EDGE",EDGE,{"disambiguationData":[OSD([sQuery(id+"F0.wireOp",EDGE,"E0.top"),sQuery(id+"F0.wireOp",EDGE,"E0.left")])]});
            var Q5;
            Q5=makeQuery(id+"F1.opExtrude","SWEPT_EDGE",EDGE,{"disambiguationData":[OSD([sQuery(id+"F0.wireOp",EDGE,"E0.bottom"),sQuery(id+"F0.wireOp",EDGE,"E0.left")])]});
            var Q6;
            Q6=makeQuery(id+"F1.opExtrude","SWEPT_EDGE",EDGE,{"disambiguationData":[OSD([sQuery(id+"F0.wireOp",EDGE,"E0.top"),sQuery(id+"F0.wireOp",EDGE,"E0.right")])]});
            var Q7;
            Q7=makeQuery(id+"F1.opExtrude","SWEPT_EDGE",EDGE,{"disambiguationData":[OSD([sQuery(id+"F0.wireOp",EDGE,"E0.bottom"),sQuery(id+"F0.wireOp",EDGE,"E0.right")])]});
            var Q8;
            Q8=makeQuery(id+"F1.opExtrude","CAP_EDGE",EDGE,{"disambiguationData":[OSD([sQuery(id+"F0.wireOp",EDGE,"E0.top")])],"isStart":true});
            var Q9;
            Q9=makeQuery(id+"F1.opExtrude","CAP_EDGE",EDGE,{"disambiguationData":[OSD([sQuery(id+"F0.wireOp",EDGE,"E0.left")])],"isStart":true});
            var Q10;
            Q10=makeQuery(id+"F1.opExtrude","CAP_EDGE",EDGE,{"disambiguationData":[OSD([sQuery(id+"F0.wireOp",EDGE,"E0.bottom")])],"isStart":true});
            var Q11;
            Q11=makeQuery(id+"F1.opExtrude","CAP_EDGE",EDGE,{"disambiguationData":[OSD([sQuery(id+"F0.wireOp",EDGE,"E0.right")])],"isStart":true});
            var Q12;
            {var subQ0=sQuery(id+"F2.wireOp",EDGE,"E7.1");var subQ1=sQuery(id+"F2.wireOp",EDGE,"E9.MirrorCS");Q12=makeQuery(id+"F30.opChamfer","BLEND_EDGE",EDGE,{"blendedFrom":[makeQuery(id+"F4.boolean.opBoolean","COPY",EDGE,{"derivedFrom":makeQuery(id+"F4.opExtrude","SWEPT_EDGE",EDGE,{"disambiguationData":[OSD([subQ0,subQ1])]})}),makeQuery(id+"F4.boolean.opBoolean","MERGE",FACE,{"derivedFrom":[makeQuery(id+"F3.boolean.opBoolean","COPY",FACE,{"derivedFrom":makeQuery(id+"F3.opExtrude","SWEPT_FACE",FACE,{"disambiguationData":[OSD([subQ0]),TDD([makeQuery(id+"F2.imprint","IMPRINT",EDGE,{"disambiguationData":[TD([[makeQuery(id+"F2.imprint","INTERSECT",VERTEX,{"derivedFrom":[sQuery(id+"F2.wireOp",EDGE,"E7.0"),subQ0]}),-1.0]])],"derivedFrom":subQ0})])]})}),makeQuery(id+"F3.boolean.opBoolean","COPY",FACE,{"derivedFrom":makeQuery(id+"F3.opExtrude","SWEPT_FACE",FACE,{"disambiguationData":[OSD([subQ0]),TDD([makeQuery(id+"F2.imprint","IMPRINT",EDGE,{"disambiguationData":[TD([[makeQuery(id+"F2.imprint","INTERSECT",VERTEX,{"derivedFrom":[subQ0,sQuery(id+"F2.wireOp",EDGE,"E7.2")]}),1.0]])],"derivedFrom":subQ0})])]})})],"fromTools":[makeQuery(id+"F4.opExtrude","SWEPT_FACE",FACE,{"disambiguationData":[OSD([subQ0])]})]})],"blendedInto":[makeQuery(id+"F4.boolean.opBoolean","MERGE",FACE,{"derivedFrom":[makeQuery(id+"F3.boolean.opBoolean","COPY",FACE,{"derivedFrom":makeQuery(id+"F3.opExtrude","SWEPT_FACE",FACE,{"disambiguationData":[OSD([subQ0]),TDD([makeQuery(id+"F2.imprint","IMPRINT",EDGE,{"disambiguationData":[TD([[makeQuery(id+"F2.imprint","INTERSECT",VERTEX,{"derivedFrom":[sQuery(id+"F2.wireOp",EDGE,"E7.0"),subQ0]}),-1.0]])],"derivedFrom":subQ0})])]})}),makeQuery(id+"F3.boolean.opBoolean","COPY",FACE,{"derivedFrom":makeQuery(id+"F3.opExtrude","SWEPT_FACE",FACE,{"disambiguationData":[OSD([subQ0]),TDD([makeQuery(id+"F2.imprint","IMPRINT",EDGE,{"disambiguationData":[TD([[makeQuery(id+"F2.imprint","INTERSECT",VERTEX,{"derivedFrom":[subQ0,sQuery(id+"F2.wireOp",EDGE,"E7.2")]}),1.0]])],"derivedFrom":subQ0})])]})})],"fromTools":[makeQuery(id+"F4.opExtrude","SWEPT_FACE",FACE,{"disambiguationData":[OSD([subQ0])]})]})]});}
            var Q13;
            {var subQ0=sQuery(id+"F2.wireOp",EDGE,"E7.2");var subQ1=sQuery(id+"F2.wireOp",EDGE,"E10.MirrorCS");Q13=makeQuery(id+"F30.opChamfer","BLEND_EDGE",EDGE,{"blendedFrom":[makeQuery(id+"F4.boolean.opBoolean","COPY",EDGE,{"derivedFrom":makeQuery(id+"F4.opExtrude","SWEPT_EDGE",EDGE,{"disambiguationData":[OSD([subQ0,subQ1])]})}),makeQuery(id+"F4.boolean.opBoolean","MERGE",FACE,{"derivedFrom":[makeQuery(id+"F3.boolean.opBoolean","COPY",FACE,{"derivedFrom":makeQuery(id+"F3.opExtrude","SWEPT_FACE",FACE,{"disambiguationData":[OSD([subQ0]),TDD([makeQuery(id+"F2.imprint","IMPRINT",EDGE,{"disambiguationData":[TD([[makeQuery(id+"F2.imprint","INTERSECT",VERTEX,{"derivedFrom":[sQuery(id+"F2.wireOp",EDGE,"E7.1"),subQ0]}),-1.0]])],"derivedFrom":subQ0})])]})}),makeQuery(id+"F3.boolean.opBoolean","COPY",FACE,{"derivedFrom":makeQuery(id+"F3.opExtrude","SWEPT_FACE",FACE,{"disambiguationData":[OSD([subQ0]),TDD([makeQuery(id+"F2.imprint","IMPRINT",EDGE,{"disambiguationData":[TD([[makeQuery(id+"F2.imprint","INTERSECT",VERTEX,{"derivedFrom":[subQ0,sQuery(id+"F2.wireOp",EDGE,"E7.3")]}),1.0]])],"derivedFrom":subQ0})])]})})],"fromTools":[makeQuery(id+"F4.opExtrude","SWEPT_FACE",FACE,{"disambiguationData":[OSD([subQ0])]})]})],"blendedInto":[makeQuery(id+"F4.boolean.opBoolean","MERGE",FACE,{"derivedFrom":[makeQuery(id+"F3.boolean.opBoolean","COPY",FACE,{"derivedFrom":makeQuery(id+"F3.opExtrude","SWEPT_FACE",FACE,{"disambiguationData":[OSD([subQ0]),TDD([makeQuery(id+"F2.imprint","IMPRINT",EDGE,{"disambiguationData":[TD([[makeQuery(id+"F2.imprint","INTERSECT",VERTEX,{"derivedFrom":[sQuery(id+"F2.wireOp",EDGE,"E7.1"),subQ0]}),-1.0]])],"derivedFrom":subQ0})])]})}),makeQuery(id+"F3.boolean.opBoolean","COPY",FACE,{"derivedFrom":makeQuery(id+"F3.opExtrude","SWEPT_FACE",FACE,{"disambiguationData":[OSD([subQ0]),TDD([makeQuery(id+"F2.imprint","IMPRINT",EDGE,{"disambiguationData":[TD([[makeQuery(id+"F2.imprint","INTERSECT",VERTEX,{"derivedFrom":[subQ0,sQuery(id+"F2.wireOp",EDGE,"E7.3")]}),1.0]])],"derivedFrom":subQ0})])]})})],"fromTools":[makeQuery(id+"F4.opExtrude","SWEPT_FACE",FACE,{"disambiguationData":[OSD([subQ0])]})]})]});}
            var Q14;
            {var subQ0=sQuery(id+"F2.wireOp",EDGE,"E7.0");var subQ1=sQuery(id+"F2.wireOp",EDGE,"E13.MirrorCS");Q14=makeQuery(id+"F30.opChamfer","BLEND_EDGE",EDGE,{"blendedFrom":[makeQuery(id+"F4.boolean.opBoolean","COPY",EDGE,{"derivedFrom":makeQuery(id+"F4.opExtrude","SWEPT_EDGE",EDGE,{"disambiguationData":[OSD([subQ0,subQ1])]})}),makeQuery(id+"F4.boolean.opBoolean","MERGE",FACE,{"derivedFrom":[makeQuery(id+"F3.boolean.opBoolean","COPY",FACE,{"derivedFrom":makeQuery(id+"F3.opExtrude","SWEPT_FACE",FACE,{"disambiguationData":[OSD([subQ0]),TDD([makeQuery(id+"F2.imprint","IMPRINT",EDGE,{"disambiguationData":[TD([[makeQuery(id+"F2.imprint","INTERSECT",VERTEX,{"derivedFrom":[subQ0,sQuery(id+"F2.wireOp",EDGE,"E7.1")]}),-1.0]])],"derivedFrom":subQ0})])]})}),makeQuery(id+"F3.boolean.opBoolean","COPY",FACE,{"derivedFrom":makeQuery(id+"F3.opExtrude","SWEPT_FACE",FACE,{"disambiguationData":[OSD([subQ0]),TDD([makeQuery(id+"F2.imprint","IMPRINT",EDGE,{"disambiguationData":[TD([[makeQuery(id+"F2.imprint","INTERSECT",VERTEX,{"derivedFrom":[subQ0,sQuery(id+"F2.wireOp",EDGE,"E7.3")]}),1.0]])],"derivedFrom":subQ0})])]})})],"fromTools":[makeQuery(id+"F4.opExtrude","SWEPT_FACE",FACE,{"disambiguationData":[OSD([subQ0])]})]})],"blendedInto":[makeQuery(id+"F4.boolean.opBoolean","MERGE",FACE,{"derivedFrom":[makeQuery(id+"F3.boolean.opBoolean","COPY",FACE,{"derivedFrom":makeQuery(id+"F3.opExtrude","SWEPT_FACE",FACE,{"disambiguationData":[OSD([subQ0]),TDD([makeQuery(id+"F2.imprint","IMPRINT",EDGE,{"disambiguationData":[TD([[makeQuery(id+"F2.imprint","INTERSECT",VERTEX,{"derivedFrom":[subQ0,sQuery(id+"F2.wireOp",EDGE,"E7.1")]}),-1.0]])],"derivedFrom":subQ0})])]})}),makeQuery(id+"F3.boolean.opBoolean","COPY",FACE,{"derivedFrom":makeQuery(id+"F3.opExtrude","SWEPT_FACE",FACE,{"disambiguationData":[OSD([subQ0]),TDD([makeQuery(id+"F2.imprint","IMPRINT",EDGE,{"disambiguationData":[TD([[makeQuery(id+"F2.imprint","INTERSECT",VERTEX,{"derivedFrom":[subQ0,sQuery(id+"F2.wireOp",EDGE,"E7.3")]}),1.0]])],"derivedFrom":subQ0})])]})})],"fromTools":[makeQuery(id+"F4.opExtrude","SWEPT_FACE",FACE,{"disambiguationData":[OSD([subQ0])]})]})]});}
            var Q15;
            {var subQ0=sQuery(id+"F2.wireOp",EDGE,"E7.1");var subQ1=sQuery(id+"F2.wireOp",EDGE,"E14.MirrorCS");Q15=makeQuery(id+"F30.opChamfer","BLEND_EDGE",EDGE,{"blendedFrom":[makeQuery(id+"F4.boolean.opBoolean","COPY",EDGE,{"derivedFrom":makeQuery(id+"F4.opExtrude","SWEPT_EDGE",EDGE,{"disambiguationData":[OSD([subQ0,subQ1])]})}),makeQuery(id+"F4.boolean.opBoolean","MERGE",FACE,{"derivedFrom":[makeQuery(id+"F3.boolean.opBoolean","COPY",FACE,{"derivedFrom":makeQuery(id+"F3.opExtrude","SWEPT_FACE",FACE,{"disambiguationData":[OSD([subQ0]),TDD([makeQuery(id+"F2.imprint","IMPRINT",EDGE,{"disambiguationData":[TD([[makeQuery(id+"F2.imprint","INTERSECT",VERTEX,{"derivedFrom":[sQuery(id+"F2.wireOp",EDGE,"E7.0"),subQ0]}),-1.0]])],"derivedFrom":subQ0})])]})}),makeQuery(id+"F3.boolean.opBoolean","COPY",FACE,{"derivedFrom":makeQuery(id+"F3.opExtrude","SWEPT_FACE",FACE,{"disambiguationData":[OSD([subQ0]),TDD([makeQuery(id+"F2.imprint","IMPRINT",EDGE,{"disambiguationData":[TD([[makeQuery(id+"F2.imprint","INTERSECT",VERTEX,{"derivedFrom":[subQ0,sQuery(id+"F2.wireOp",EDGE,"E7.2")]}),1.0]])],"derivedFrom":subQ0})])]})})],"fromTools":[makeQuery(id+"F4.opExtrude","SWEPT_FACE",FACE,{"disambiguationData":[OSD([subQ0])]})]})],"blendedInto":[makeQuery(id+"F4.boolean.opBoolean","MERGE",FACE,{"derivedFrom":[makeQuery(id+"F3.boolean.opBoolean","COPY",FACE,{"derivedFrom":makeQuery(id+"F3.opExtrude","SWEPT_FACE",FACE,{"disambiguationData":[OSD([subQ0]),TDD([makeQuery(id+"F2.imprint","IMPRINT",EDGE,{"disambiguationData":[TD([[makeQuery(id+"F2.imprint","INTERSECT",VERTEX,{"derivedFrom":[sQuery(id+"F2.wireOp",EDGE,"E7.0"),subQ0]}),-1.0]])],"derivedFrom":subQ0})])]})}),makeQuery(id+"F3.boolean.opBoolean","COPY",FACE,{"derivedFrom":makeQuery(id+"F3.opExtrude","SWEPT_FACE",FACE,{"disambiguationData":[OSD([subQ0]),TDD([makeQuery(id+"F2.imprint","IMPRINT",EDGE,{"disambiguationData":[TD([[makeQuery(id+"F2.imprint","INTERSECT",VERTEX,{"derivedFrom":[subQ0,sQuery(id+"F2.wireOp",EDGE,"E7.2")]}),1.0]])],"derivedFrom":subQ0})])]})})],"fromTools":[makeQuery(id+"F4.opExtrude","SWEPT_FACE",FACE,{"disambiguationData":[OSD([subQ0])]})]})]});}
            var Q16;
            {var subQ0=sQuery(id+"F2.wireOp",EDGE,"E7.3");var subQ1=sQuery(id+"F2.wireOp",EDGE,"E12.MirrorCS");Q16=makeQuery(id+"F30.opChamfer","BLEND_EDGE",EDGE,{"blendedFrom":[makeQuery(id+"F4.boolean.opBoolean","COPY",EDGE,{"derivedFrom":makeQuery(id+"F4.opExtrude","SWEPT_EDGE",EDGE,{"disambiguationData":[OSD([subQ0,subQ1])]})}),makeQuery(id+"F4.boolean.opBoolean","MERGE",FACE,{"derivedFrom":[makeQuery(id+"F3.boolean.opBoolean","COPY",FACE,{"derivedFrom":makeQuery(id+"F3.opExtrude","SWEPT_FACE",FACE,{"disambiguationData":[OSD([subQ0]),TDD([makeQuery(id+"F2.imprint","IMPRINT",EDGE,{"disambiguationData":[TD([[makeQuery(id+"F2.imprint","INTERSECT",VERTEX,{"derivedFrom":[sQuery(id+"F2.wireOp",EDGE,"E7.0"),subQ0]}),-1.0]])],"derivedFrom":subQ0})])]})}),makeQuery(id+"F3.boolean.opBoolean","COPY",FACE,{"derivedFrom":makeQuery(id+"F3.opExtrude","SWEPT_FACE",FACE,{"disambiguationData":[OSD([subQ0]),TDD([makeQuery(id+"F2.imprint","IMPRINT",EDGE,{"disambiguationData":[TD([[makeQuery(id+"F2.imprint","INTERSECT",VERTEX,{"derivedFrom":[sQuery(id+"F2.wireOp",EDGE,"E7.2"),subQ0]}),1.0]])],"derivedFrom":subQ0})])]})})],"fromTools":[makeQuery(id+"F4.opExtrude","SWEPT_FACE",FACE,{"disambiguationData":[OSD([subQ0])]})]})],"blendedInto":[makeQuery(id+"F4.boolean.opBoolean","MERGE",FACE,{"derivedFrom":[makeQuery(id+"F3.boolean.opBoolean","COPY",FACE,{"derivedFrom":makeQuery(id+"F3.opExtrude","SWEPT_FACE",FACE,{"disambiguationData":[OSD([subQ0]),TDD([makeQuery(id+"F2.imprint","IMPRINT",EDGE,{"disambiguationData":[TD([[makeQuery(id+"F2.imprint","INTERSECT",VERTEX,{"derivedFrom":[sQuery(id+"F2.wireOp",EDGE,"E7.0"),subQ0]}),-1.0]])],"derivedFrom":subQ0})])]})}),makeQuery(id+"F3.boolean.opBoolean","COPY",FACE,{"derivedFrom":makeQuery(id+"F3.opExtrude","SWEPT_FACE",FACE,{"disambiguationData":[OSD([subQ0]),TDD([makeQuery(id+"F2.imprint","IMPRINT",EDGE,{"disambiguationData":[TD([[makeQuery(id+"F2.imprint","INTERSECT",VERTEX,{"derivedFrom":[sQuery(id+"F2.wireOp",EDGE,"E7.2"),subQ0]}),1.0]])],"derivedFrom":subQ0})])]})})],"fromTools":[makeQuery(id+"F4.opExtrude","SWEPT_FACE",FACE,{"disambiguationData":[OSD([subQ0])]})]})]});}
            var Q17;
            {var subQ0=sQuery(id+"F2.wireOp",EDGE,"E7.0");var subQ1=sQuery(id+"F2.wireOp",EDGE,"E11.MirrorCS");Q17=makeQuery(id+"F30.opChamfer","BLEND_EDGE",EDGE,{"blendedFrom":[makeQuery(id+"F4.boolean.opBoolean","COPY",EDGE,{"derivedFrom":makeQuery(id+"F4.opExtrude","SWEPT_EDGE",EDGE,{"disambiguationData":[OSD([subQ0,subQ1])]})}),makeQuery(id+"F4.boolean.opBoolean","MERGE",FACE,{"derivedFrom":[makeQuery(id+"F3.boolean.opBoolean","COPY",FACE,{"derivedFrom":makeQuery(id+"F3.opExtrude","SWEPT_FACE",FACE,{"disambiguationData":[OSD([subQ0]),TDD([makeQuery(id+"F2.imprint","IMPRINT",EDGE,{"disambiguationData":[TD([[makeQuery(id+"F2.imprint","INTERSECT",VERTEX,{"derivedFrom":[subQ0,sQuery(id+"F2.wireOp",EDGE,"E7.1")]}),-1.0]])],"derivedFrom":subQ0})])]})}),makeQuery(id+"F3.boolean.opBoolean","COPY",FACE,{"derivedFrom":makeQuery(id+"F3.opExtrude","SWEPT_FACE",FACE,{"disambiguationData":[OSD([subQ0]),TDD([makeQuery(id+"F2.imprint","IMPRINT",EDGE,{"disambiguationData":[TD([[makeQuery(id+"F2.imprint","INTERSECT",VERTEX,{"derivedFrom":[subQ0,sQuery(id+"F2.wireOp",EDGE,"E7.3")]}),1.0]])],"derivedFrom":subQ0})])]})})],"fromTools":[makeQuery(id+"F4.opExtrude","SWEPT_FACE",FACE,{"disambiguationData":[OSD([subQ0])]})]})],"blendedInto":[makeQuery(id+"F4.boolean.opBoolean","MERGE",FACE,{"derivedFrom":[makeQuery(id+"F3.boolean.opBoolean","COPY",FACE,{"derivedFrom":makeQuery(id+"F3.opExtrude","SWEPT_FACE",FACE,{"disambiguationData":[OSD([subQ0]),TDD([makeQuery(id+"F2.imprint","IMPRINT",EDGE,{"disambiguationData":[TD([[makeQuery(id+"F2.imprint","INTERSECT",VERTEX,{"derivedFrom":[subQ0,sQuery(id+"F2.wireOp",EDGE,"E7.1")]}),-1.0]])],"derivedFrom":subQ0})])]})}),makeQuery(id+"F3.boolean.opBoolean","COPY",FACE,{"derivedFrom":makeQuery(id+"F3.opExtrude","SWEPT_FACE",FACE,{"disambiguationData":[OSD([subQ0]),TDD([makeQuery(id+"F2.imprint","IMPRINT",EDGE,{"disambiguationData":[TD([[makeQuery(id+"F2.imprint","INTERSECT",VERTEX,{"derivedFrom":[subQ0,sQuery(id+"F2.wireOp",EDGE,"E7.3")]}),1.0]])],"derivedFrom":subQ0})])]})})],"fromTools":[makeQuery(id+"F4.opExtrude","SWEPT_FACE",FACE,{"disambiguationData":[OSD([subQ0])]})]})]});}
            var Q18;
            {var subQ0=sQuery(id+"F2.wireOp",EDGE,"E7.2");var subQ1=sQuery(id+"F2.wireOp",EDGE,"E8.top");Q18=makeQuery(id+"F30.opChamfer","BLEND_EDGE",EDGE,{"blendedFrom":[makeQuery(id+"F4.boolean.opBoolean","COPY",EDGE,{"derivedFrom":makeQuery(id+"F4.opExtrude","SWEPT_EDGE",EDGE,{"disambiguationData":[OSD([subQ0,subQ1])]})}),makeQuery(id+"F4.boolean.opBoolean","MERGE",FACE,{"derivedFrom":[makeQuery(id+"F3.boolean.opBoolean","COPY",FACE,{"derivedFrom":makeQuery(id+"F3.opExtrude","SWEPT_FACE",FACE,{"disambiguationData":[OSD([subQ0]),TDD([makeQuery(id+"F2.imprint","IMPRINT",EDGE,{"disambiguationData":[TD([[makeQuery(id+"F2.imprint","INTERSECT",VERTEX,{"derivedFrom":[sQuery(id+"F2.wireOp",EDGE,"E7.1"),subQ0]}),-1.0]])],"derivedFrom":subQ0})])]})}),makeQuery(id+"F3.boolean.opBoolean","COPY",FACE,{"derivedFrom":makeQuery(id+"F3.opExtrude","SWEPT_FACE",FACE,{"disambiguationData":[OSD([subQ0]),TDD([makeQuery(id+"F2.imprint","IMPRINT",EDGE,{"disambiguationData":[TD([[makeQuery(id+"F2.imprint","INTERSECT",VERTEX,{"derivedFrom":[subQ0,sQuery(id+"F2.wireOp",EDGE,"E7.3")]}),1.0]])],"derivedFrom":subQ0})])]})})],"fromTools":[makeQuery(id+"F4.opExtrude","SWEPT_FACE",FACE,{"disambiguationData":[OSD([subQ0])]})]})],"blendedInto":[makeQuery(id+"F4.boolean.opBoolean","MERGE",FACE,{"derivedFrom":[makeQuery(id+"F3.boolean.opBoolean","COPY",FACE,{"derivedFrom":makeQuery(id+"F3.opExtrude","SWEPT_FACE",FACE,{"disambiguationData":[OSD([subQ0]),TDD([makeQuery(id+"F2.imprint","IMPRINT",EDGE,{"disambiguationData":[TD([[makeQuery(id+"F2.imprint","INTERSECT",VERTEX,{"derivedFrom":[sQuery(id+"F2.wireOp",EDGE,"E7.1"),subQ0]}),-1.0]])],"derivedFrom":subQ0})])]})}),makeQuery(id+"F3.boolean.opBoolean","COPY",FACE,{"derivedFrom":makeQuery(id+"F3.opExtrude","SWEPT_FACE",FACE,{"disambiguationData":[OSD([subQ0]),TDD([makeQuery(id+"F2.imprint","IMPRINT",EDGE,{"disambiguationData":[TD([[makeQuery(id+"F2.imprint","INTERSECT",VERTEX,{"derivedFrom":[subQ0,sQuery(id+"F2.wireOp",EDGE,"E7.3")]}),1.0]])],"derivedFrom":subQ0})])]})})],"fromTools":[makeQuery(id+"F4.opExtrude","SWEPT_FACE",FACE,{"disambiguationData":[OSD([subQ0])]})]})]});}
            var Q19;
            {var subQ0=sQuery(id+"F2.wireOp",EDGE,"E7.3");var subQ1=sQuery(id+"F2.wireOp",EDGE,"E8.right");Q19=makeQuery(id+"F30.opChamfer","BLEND_EDGE",EDGE,{"blendedFrom":[makeQuery(id+"F4.boolean.opBoolean","COPY",EDGE,{"derivedFrom":makeQuery(id+"F4.opExtrude","SWEPT_EDGE",EDGE,{"disambiguationData":[OSD([subQ0,subQ1])]})}),makeQuery(id+"F4.boolean.opBoolean","MERGE",FACE,{"derivedFrom":[makeQuery(id+"F3.boolean.opBoolean","COPY",FACE,{"derivedFrom":makeQuery(id+"F3.opExtrude","SWEPT_FACE",FACE,{"disambiguationData":[OSD([subQ0]),TDD([makeQuery(id+"F2.imprint","IMPRINT",EDGE,{"disambiguationData":[TD([[makeQuery(id+"F2.imprint","INTERSECT",VERTEX,{"derivedFrom":[sQuery(id+"F2.wireOp",EDGE,"E7.0"),subQ0]}),-1.0]])],"derivedFrom":subQ0})])]})}),makeQuery(id+"F3.boolean.opBoolean","COPY",FACE,{"derivedFrom":makeQuery(id+"F3.opExtrude","SWEPT_FACE",FACE,{"disambiguationData":[OSD([subQ0]),TDD([makeQuery(id+"F2.imprint","IMPRINT",EDGE,{"disambiguationData":[TD([[makeQuery(id+"F2.imprint","INTERSECT",VERTEX,{"derivedFrom":[sQuery(id+"F2.wireOp",EDGE,"E7.2"),subQ0]}),1.0]])],"derivedFrom":subQ0})])]})})],"fromTools":[makeQuery(id+"F4.opExtrude","SWEPT_FACE",FACE,{"disambiguationData":[OSD([subQ0])]})]})],"blendedInto":[makeQuery(id+"F4.boolean.opBoolean","MERGE",FACE,{"derivedFrom":[makeQuery(id+"F3.boolean.opBoolean","COPY",FACE,{"derivedFrom":makeQuery(id+"F3.opExtrude","SWEPT_FACE",FACE,{"disambiguationData":[OSD([subQ0]),TDD([makeQuery(id+"F2.imprint","IMPRINT",EDGE,{"disambiguationData":[TD([[makeQuery(id+"F2.imprint","INTERSECT",VERTEX,{"derivedFrom":[sQuery(id+"F2.wireOp",EDGE,"E7.0"),subQ0]}),-1.0]])],"derivedFrom":subQ0})])]})}),makeQuery(id+"F3.boolean.opBoolean","COPY",FACE,{"derivedFrom":makeQuery(id+"F3.opExtrude","SWEPT_FACE",FACE,{"disambiguationData":[OSD([subQ0]),TDD([makeQuery(id+"F2.imprint","IMPRINT",EDGE,{"disambiguationData":[TD([[makeQuery(id+"F2.imprint","INTERSECT",VERTEX,{"derivedFrom":[sQuery(id+"F2.wireOp",EDGE,"E7.2"),subQ0]}),1.0]])],"derivedFrom":subQ0})])]})})],"fromTools":[makeQuery(id+"F4.opExtrude","SWEPT_FACE",FACE,{"disambiguationData":[OSD([subQ0])]})]})]});}
            var Q20;
            Q20=makeQuery(id+"F1.opExtrude","SWEPT_FACE",FACE,{"disambiguationData":[OSD([sQuery(id+"F0.wireOp",EDGE,"qKKrQyln-KT76-C0dK-uMFZ-fzOofCrcuMC0")])]});
            var Q21;
            Q21=makeQuery(id+"F1.opExtrude","SWEPT_FACE",FACE,{"disambiguationData":[OSD([sQuery(id+"F0.wireOp",EDGE,"E1.top")])]});
            var Q22;
            Q22=makeQuery(id+"F1.opExtrude","SWEPT_FACE",FACE,{"disambiguationData":[OSD([sQuery(id+"F0.wireOp",EDGE,"E1.bottom")])]});
            var Q23;
            {var subQ0=sQuery(id+"F2.wireOp",EDGE,"E7.3");Q23=makeQuery(id+"F10.boolean.opBoolean","INTERSECT",EDGE,{"derivedFrom":[makeQuery(id+"F4.boolean.opBoolean","MERGE",FACE,{"derivedFrom":[makeQuery(id+"F3.boolean.opBoolean","COPY",FACE,{"derivedFrom":makeQuery(id+"F3.opExtrude","SWEPT_FACE",FACE,{"disambiguationData":[OSD([subQ0]),TDD([makeQuery(id+"F2.imprint","IMPRINT",EDGE,{"disambiguationData":[TD([[makeQuery(id+"F2.imprint","INTERSECT",VERTEX,{"derivedFrom":[sQuery(id+"F2.wireOp",EDGE,"E7.0"),subQ0]}),-1.0]])],"derivedFrom":subQ0})])]})}),makeQuery(id+"F3.boolean.opBoolean","COPY",FACE,{"derivedFrom":makeQuery(id+"F3.opExtrude","SWEPT_FACE",FACE,{"disambiguationData":[OSD([subQ0]),TDD([makeQuery(id+"F2.imprint","IMPRINT",EDGE,{"disambiguationData":[TD([[makeQuery(id+"F2.imprint","INTERSECT",VERTEX,{"derivedFrom":[sQuery(id+"F2.wireOp",EDGE,"E7.2"),subQ0]}),1.0]])],"derivedFrom":subQ0})])]})})],"fromTools":[makeQuery(id+"F4.opExtrude","SWEPT_FACE",FACE,{"disambiguationData":[OSD([subQ0])]})]}),makeQuery(id+"F10.opExtrude","SWEPT_FACE",FACE,{"disambiguationData":[OSD([sQuery(id+"F8.wireOp",EDGE,"E109.1")])]})]});}
            fillet(context, id + "F32", {"entities" : qUnion([Q0, Q1, Q2, Q3, Q4, Q5, Q6, Q7, Q8, Q9, Q10, Q11, Q12, Q13, Q14, Q15, Q16, Q17, Q18, Q19, Q20, Q21, Q22, Q23]), "radius" : 3.17 * mm, "tangentPropagation" : true, "allowEdgeOverflow" : false});
        }
        {
            var Q0;
            {var subQ10=sQuery(id+"F0.wireOp",EDGE,"E0.bottom");var subQ13=sQuery(id+"F0.wireOp",EDGE,"E0.right");var subQ16=sQuery(id+"F0.wireOp",EDGE,"E0.top");var subQ18=sQuery(id+"F0.wireOp",EDGE,"E0.left");Q0=makeQuery(id+"F3.boolean.opBoolean","SPLIT",FACE,{"disambiguationData":[TD([makeQuery(id+"F1.opExtrude","SWEPT_FACE",FACE,{"disambiguationData":[OSD([subQ10])]})])],"derivedFrom":makeQuery(id+"F1.opExtrude","CAP_FACE",FACE,{"disambiguationData":[OSD([subQ10,subQ16,subQ18,subQ13])],"isStart":false})});}
            var Q1;
            Q1=makeQuery(id+"F1.opExtrude","SWEPT_FACE",FACE,{"disambiguationData":[OSD([sQuery(id+"F0.wireOp",EDGE,"E0.right")])]});
            var Q2;
            Q2=makeQuery(id+"F1.opExtrude","SWEPT_FACE",FACE,{"disambiguationData":[OSD([sQuery(id+"F0.wireOp",EDGE,"E0.top")])]});
            var Q3;
            Q3=makeQuery(id+"F1.opExtrude","SWEPT_FACE",FACE,{"disambiguationData":[OSD([sQuery(id+"F0.wireOp",EDGE,"E0.bottom")])]});
            var Q4;
            Q4=makeQuery(id+"F1.opExtrude","SWEPT_FACE",FACE,{"disambiguationData":[OSD([sQuery(id+"F0.wireOp",EDGE,"E0.left")])]});
            var Q5;
            {var subQ0=sQuery(id+"F5.wireOp",EDGE,"E28.2");Q5=makeQuery(id+"F22.boolean.opBoolean","MERGE",EDGE,{"derivedFrom":[makeQuery(id+"F12.boolean.opBoolean","INTERSECT",EDGE,{"derivedFrom":[makeQuery(id+"F9.boolean.opBoolean","COPY",FACE,{"derivedFrom":makeQuery(id+"F9.opExtrude","SWEPT_FACE",FACE,{"disambiguationData":[OSD([subQ0])]})}),makeQuery(id+"F12.opExtrude","SWEPT_FACE",FACE,{"disambiguationData":[OSD([sQuery(id+"F6.wireOp",EDGE,"E68.bottom")])]})]})],"fromTools":[makeQuery(id+"F22.opExtrude","SWEPT_EDGE",EDGE,{"disambiguationData":[OSD([subQ0,sQuery(id+"F5.wireOp",EDGE,"E36.MirrorCS")])]})]});}
            var Q6;
            {var subQ0=sQuery(id+"F5.wireOp",EDGE,"E28.2");Q6=makeQuery(id+"F22.boolean.opBoolean","MERGE",EDGE,{"derivedFrom":[makeQuery(id+"F12.boolean.opBoolean","INTERSECT",EDGE,{"derivedFrom":[makeQuery(id+"F9.boolean.opBoolean","COPY",FACE,{"derivedFrom":makeQuery(id+"F9.opExtrude","SWEPT_FACE",FACE,{"disambiguationData":[OSD([subQ0])]})}),makeQuery(id+"F12.opExtrude","SWEPT_FACE",FACE,{"disambiguationData":[OSD([sQuery(id+"F6.wireOp",EDGE,"E68.top")])]})]})],"fromTools":[makeQuery(id+"F22.opExtrude","SWEPT_EDGE",EDGE,{"disambiguationData":[OSD([subQ0,sQuery(id+"F5.wireOp",EDGE,"E38.MirrorCS")])]})]});}
            var Q7;
            Q7=makeQuery(id+"F12.boolean.opBoolean","COPY",EDGE,{"derivedFrom":makeQuery(id+"F12.opExtrude","SWEPT_EDGE",EDGE,{"disambiguationData":[OSD([sQuery(id+"F6.wireOp",EDGE,"E54.0"),sQuery(id+"F6.wireOp",EDGE,"E68.bottom"),sQuery(id+"F6.wireOp",EDGE,"E68.right")])]})});
            var Q8;
            Q8=makeQuery(id+"F12.boolean.opBoolean","COPY",EDGE,{"derivedFrom":makeQuery(id+"F12.opExtrude","SWEPT_EDGE",EDGE,{"disambiguationData":[OSD([sQuery(id+"F6.wireOp",EDGE,"E54.0"),sQuery(id+"F6.wireOp",EDGE,"E68.top"),sQuery(id+"F6.wireOp",EDGE,"E68.right")])]})});
            var Q9;
            {var subQ0=sQuery(id+"F8.wireOp",EDGE,"E109.2");Q9=makeQuery(id+"F25.boolean.opBoolean","MERGE",EDGE,{"derivedFrom":[makeQuery(id+"F10.boolean.opBoolean","INTERSECT",EDGE,{"derivedFrom":[makeQuery(id+"F9.boolean.opBoolean","COPY",FACE,{"derivedFrom":makeQuery(id+"F9.opExtrude","SWEPT_FACE",FACE,{"disambiguationData":[OSD([sQuery(id+"F5.wireOp",EDGE,"E42.top")])]})}),makeQuery(id+"F10.opExtrude","SWEPT_FACE",FACE,{"disambiguationData":[OSD([subQ0])]})]})],"fromTools":[makeQuery(id+"F25.opExtrude","SWEPT_EDGE",EDGE,{"disambiguationData":[OSD([subQ0,sQuery(id+"F8.wireOp",EDGE,"E119.MirrorCS")])]})]});}
            var Q10;
            {var subQ0=sQuery(id+"F8.wireOp",EDGE,"E109.2");Q10=makeQuery(id+"F25.boolean.opBoolean","MERGE",EDGE,{"derivedFrom":[makeQuery(id+"F10.boolean.opBoolean","INTERSECT",EDGE,{"derivedFrom":[makeQuery(id+"F9.boolean.opBoolean","COPY",FACE,{"derivedFrom":makeQuery(id+"F9.opExtrude","SWEPT_FACE",FACE,{"disambiguationData":[OSD([sQuery(id+"F5.wireOp",EDGE,"E42.bottom")])]})}),makeQuery(id+"F10.opExtrude","SWEPT_FACE",FACE,{"disambiguationData":[OSD([subQ0])]})]})],"fromTools":[makeQuery(id+"F25.opExtrude","SWEPT_EDGE",EDGE,{"disambiguationData":[OSD([subQ0,sQuery(id+"F8.wireOp",EDGE,"E117.MirrorCS")])]})]});}
            var Q11;
            Q11=makeQuery(id+"F9.boolean.opBoolean","COPY",EDGE,{"derivedFrom":makeQuery(id+"F9.opExtrude","SWEPT_EDGE",EDGE,{"disambiguationData":[OSD([sQuery(id+"F5.wireOp",EDGE,"E28.0"),sQuery(id+"F5.wireOp",EDGE,"E42.bottom"),sQuery(id+"F5.wireOp",EDGE,"E42.right")])]})});
            var Q12;
            Q12=makeQuery(id+"F9.boolean.opBoolean","COPY",EDGE,{"derivedFrom":makeQuery(id+"F9.opExtrude","SWEPT_EDGE",EDGE,{"disambiguationData":[OSD([sQuery(id+"F5.wireOp",EDGE,"E28.0"),sQuery(id+"F5.wireOp",EDGE,"E42.top"),sQuery(id+"F5.wireOp",EDGE,"E42.right")])]})});
            var Q13;
            Q13=makeQuery(id+"F10.boolean.opBoolean","COPY",EDGE,{"derivedFrom":makeQuery(id+"F10.opExtrude","SWEPT_EDGE",EDGE,{"disambiguationData":[OSD([sQuery(id+"F8.wireOp",EDGE,"E109.0"),sQuery(id+"F8.wireOp",EDGE,"E123.bottom"),sQuery(id+"F8.wireOp",EDGE,"E123.right")])]})});
            var Q14;
            {var subQ0=sQuery(id+"F7.wireOp",EDGE,"E83.2");Q14=makeQuery(id+"F24.boolean.opBoolean","MERGE",EDGE,{"derivedFrom":[makeQuery(id+"F11.boolean.opBoolean","INTERSECT",EDGE,{"derivedFrom":[makeQuery(id+"F10.boolean.opBoolean","COPY",FACE,{"derivedFrom":makeQuery(id+"F10.opExtrude","SWEPT_FACE",FACE,{"disambiguationData":[OSD([sQuery(id+"F8.wireOp",EDGE,"E123.bottom")])]})}),makeQuery(id+"F11.opExtrude","SWEPT_FACE",FACE,{"disambiguationData":[OSD([subQ0])]})]})],"fromTools":[makeQuery(id+"F24.opExtrude","SWEPT_EDGE",EDGE,{"disambiguationData":[OSD([subQ0,sQuery(id+"F7.wireOp",EDGE,"E91.MirrorCS")])]})]});}
            var Q15;
            {var subQ0=sQuery(id+"F7.wireOp",EDGE,"E83.2");Q15=makeQuery(id+"F24.boolean.opBoolean","MERGE",EDGE,{"derivedFrom":[makeQuery(id+"F11.boolean.opBoolean","INTERSECT",EDGE,{"derivedFrom":[makeQuery(id+"F10.boolean.opBoolean","COPY",FACE,{"derivedFrom":makeQuery(id+"F10.opExtrude","SWEPT_FACE",FACE,{"disambiguationData":[OSD([sQuery(id+"F8.wireOp",EDGE,"E123.top")])]})}),makeQuery(id+"F11.opExtrude","SWEPT_FACE",FACE,{"disambiguationData":[OSD([subQ0])]})]})],"fromTools":[makeQuery(id+"F24.opExtrude","SWEPT_EDGE",EDGE,{"disambiguationData":[OSD([subQ0,sQuery(id+"F7.wireOp",EDGE,"E93.MirrorCS")])]})]});}
            var Q16;
            Q16=makeQuery(id+"F10.boolean.opBoolean","COPY",EDGE,{"derivedFrom":makeQuery(id+"F10.opExtrude","SWEPT_EDGE",EDGE,{"disambiguationData":[OSD([sQuery(id+"F8.wireOp",EDGE,"E109.0"),sQuery(id+"F8.wireOp",EDGE,"E123.top"),sQuery(id+"F8.wireOp",EDGE,"E123.right")])]})});
            var Q17;
            {var subQ0=sQuery(id+"F6.wireOp",EDGE,"E54.2");Q17=makeQuery(id+"F23.boolean.opBoolean","MERGE",EDGE,{"derivedFrom":[makeQuery(id+"F12.boolean.opBoolean","INTERSECT",EDGE,{"derivedFrom":[makeQuery(id+"F11.boolean.opBoolean","COPY",FACE,{"derivedFrom":makeQuery(id+"F11.opExtrude","SWEPT_FACE",FACE,{"disambiguationData":[OSD([sQuery(id+"F7.wireOp",EDGE,"E97.bottom")])]})}),makeQuery(id+"F12.opExtrude","SWEPT_FACE",FACE,{"disambiguationData":[OSD([subQ0])]})]})],"fromTools":[makeQuery(id+"F23.opExtrude","SWEPT_EDGE",EDGE,{"disambiguationData":[OSD([subQ0,sQuery(id+"F6.wireOp",EDGE,"E62.MirrorCS")])]})]});}
            var Q18;
            Q18=makeQuery(id+"F11.boolean.opBoolean","COPY",EDGE,{"derivedFrom":makeQuery(id+"F11.opExtrude","SWEPT_EDGE",EDGE,{"disambiguationData":[OSD([sQuery(id+"F7.wireOp",EDGE,"E83.0"),sQuery(id+"F7.wireOp",EDGE,"E97.bottom"),sQuery(id+"F7.wireOp",EDGE,"E97.right")])]})});
            var Q19;
            Q19=makeQuery(id+"F11.boolean.opBoolean","COPY",EDGE,{"derivedFrom":makeQuery(id+"F11.opExtrude","SWEPT_EDGE",EDGE,{"disambiguationData":[OSD([sQuery(id+"F7.wireOp",EDGE,"E83.0"),sQuery(id+"F7.wireOp",EDGE,"E97.top"),sQuery(id+"F7.wireOp",EDGE,"E97.right")])]})});
            var Q20;
            {var subQ0=sQuery(id+"F6.wireOp",EDGE,"E54.2");Q20=makeQuery(id+"F23.boolean.opBoolean","MERGE",EDGE,{"derivedFrom":[makeQuery(id+"F12.boolean.opBoolean","INTERSECT",EDGE,{"derivedFrom":[makeQuery(id+"F11.boolean.opBoolean","COPY",FACE,{"derivedFrom":makeQuery(id+"F11.opExtrude","SWEPT_FACE",FACE,{"disambiguationData":[OSD([sQuery(id+"F7.wireOp",EDGE,"E97.top")])]})}),makeQuery(id+"F12.opExtrude","SWEPT_FACE",FACE,{"disambiguationData":[OSD([subQ0])]})]})],"fromTools":[makeQuery(id+"F23.opExtrude","SWEPT_EDGE",EDGE,{"disambiguationData":[OSD([subQ0,sQuery(id+"F6.wireOp",EDGE,"E64.MirrorCS")])]})]});}
            var Q21;
            {var subQ0=sQuery(id+"F2.wireOp",EDGE,"E7.2");Q21=makeQuery(id+"F12.boolean.opBoolean","INTERSECT",EDGE,{"derivedFrom":[makeQuery(id+"F4.boolean.opBoolean","MERGE",FACE,{"derivedFrom":[makeQuery(id+"F3.boolean.opBoolean","COPY",FACE,{"derivedFrom":makeQuery(id+"F3.opExtrude","SWEPT_FACE",FACE,{"disambiguationData":[OSD([subQ0]),TDD([makeQuery(id+"F2.imprint","IMPRINT",EDGE,{"disambiguationData":[TD([[makeQuery(id+"F2.imprint","INTERSECT",VERTEX,{"derivedFrom":[sQuery(id+"F2.wireOp",EDGE,"E7.1"),subQ0]}),-1.0]])],"derivedFrom":subQ0})])]})}),makeQuery(id+"F3.boolean.opBoolean","COPY",FACE,{"derivedFrom":makeQuery(id+"F3.opExtrude","SWEPT_FACE",FACE,{"disambiguationData":[OSD([subQ0]),TDD([makeQuery(id+"F2.imprint","IMPRINT",EDGE,{"disambiguationData":[TD([[makeQuery(id+"F2.imprint","INTERSECT",VERTEX,{"derivedFrom":[subQ0,sQuery(id+"F2.wireOp",EDGE,"E7.3")]}),1.0]])],"derivedFrom":subQ0})])]})})],"fromTools":[makeQuery(id+"F4.opExtrude","SWEPT_FACE",FACE,{"disambiguationData":[OSD([subQ0])]})]}),makeQuery(id+"F12.opExtrude","SWEPT_FACE",FACE,{"disambiguationData":[OSD([sQuery(id+"F6.wireOp",EDGE,"E71.right")])]})]});}
            var Q22;
            {var subQ0=sQuery(id+"F2.wireOp",EDGE,"E7.2");Q22=makeQuery(id+"F26.boolean.opBoolean","MERGE",EDGE,{"derivedFrom":[makeQuery(id+"F12.boolean.opBoolean","INTERSECT",EDGE,{"derivedFrom":[makeQuery(id+"F4.boolean.opBoolean","MERGE",FACE,{"derivedFrom":[makeQuery(id+"F3.boolean.opBoolean","COPY",FACE,{"derivedFrom":makeQuery(id+"F3.opExtrude","SWEPT_FACE",FACE,{"disambiguationData":[OSD([subQ0]),TDD([makeQuery(id+"F2.imprint","IMPRINT",EDGE,{"disambiguationData":[TD([[makeQuery(id+"F2.imprint","INTERSECT",VERTEX,{"derivedFrom":[sQuery(id+"F2.wireOp",EDGE,"E7.1"),subQ0]}),-1.0]])],"derivedFrom":subQ0})])]})}),makeQuery(id+"F3.boolean.opBoolean","COPY",FACE,{"derivedFrom":makeQuery(id+"F3.opExtrude","SWEPT_FACE",FACE,{"disambiguationData":[OSD([subQ0]),TDD([makeQuery(id+"F2.imprint","IMPRINT",EDGE,{"disambiguationData":[TD([[makeQuery(id+"F2.imprint","INTERSECT",VERTEX,{"derivedFrom":[subQ0,sQuery(id+"F2.wireOp",EDGE,"E7.3")]}),1.0]])],"derivedFrom":subQ0})])]})})],"fromTools":[makeQuery(id+"F4.opExtrude","SWEPT_FACE",FACE,{"disambiguationData":[OSD([subQ0])]})]}),makeQuery(id+"F12.opExtrude","SWEPT_FACE",FACE,{"disambiguationData":[OSD([sQuery(id+"F6.wireOp",EDGE,"E71.top")])]})]})],"fromTools":[makeQuery(id+"F26.opExtrude","SWEPT_EDGE",EDGE,{"disambiguationData":[OSD([subQ0,sQuery(id+"F2.wireOp",EDGE,"E19.MirrorCS")])]})]});}
            var Q23;
            {var subQ0=sQuery(id+"F2.wireOp",EDGE,"E7.2");Q23=makeQuery(id+"F26.boolean.opBoolean","MERGE",EDGE,{"derivedFrom":[makeQuery(id+"F12.boolean.opBoolean","INTERSECT",EDGE,{"derivedFrom":[makeQuery(id+"F4.boolean.opBoolean","MERGE",FACE,{"derivedFrom":[makeQuery(id+"F3.boolean.opBoolean","COPY",FACE,{"derivedFrom":makeQuery(id+"F3.opExtrude","SWEPT_FACE",FACE,{"disambiguationData":[OSD([subQ0]),TDD([makeQuery(id+"F2.imprint","IMPRINT",EDGE,{"disambiguationData":[TD([[makeQuery(id+"F2.imprint","INTERSECT",VERTEX,{"derivedFrom":[sQuery(id+"F2.wireOp",EDGE,"E7.1"),subQ0]}),-1.0]])],"derivedFrom":subQ0})])]})}),makeQuery(id+"F3.boolean.opBoolean","COPY",FACE,{"derivedFrom":makeQuery(id+"F3.opExtrude","SWEPT_FACE",FACE,{"disambiguationData":[OSD([subQ0]),TDD([makeQuery(id+"F2.imprint","IMPRINT",EDGE,{"disambiguationData":[TD([[makeQuery(id+"F2.imprint","INTERSECT",VERTEX,{"derivedFrom":[subQ0,sQuery(id+"F2.wireOp",EDGE,"E7.3")]}),1.0]])],"derivedFrom":subQ0})])]})})],"fromTools":[makeQuery(id+"F4.opExtrude","SWEPT_FACE",FACE,{"disambiguationData":[OSD([subQ0])]})]}),makeQuery(id+"F12.opExtrude","SWEPT_FACE",FACE,{"disambiguationData":[OSD([sQuery(id+"F6.wireOp",EDGE,"E71.bottom")])]})]})],"fromTools":[makeQuery(id+"F26.opExtrude","SWEPT_EDGE",EDGE,{"disambiguationData":[OSD([subQ0,sQuery(id+"F2.wireOp",EDGE,"E16.MirrorCS")])]})]});}
            var Q24;
            {var subQ0=sQuery(id+"F28.wireOp",EDGE,"E132.top");var subQ1=sQuery(id+"F28.wireOp",EDGE,"E132.right");Q24=makeQuery(id+"F29.boolean.opBoolean","COPY",EDGE,{"disambiguationData":[TD([makeQuery(id+"F11.boolean.opBoolean","COPY",FACE,{"derivedFrom":makeQuery(id+"F11.opExtrude","SWEPT_FACE",FACE,{"disambiguationData":[OSD([sQuery(id+"F7.wireOp",EDGE,"E89.MirrorCS")])]})})])],"derivedFrom":makeQuery(id+"F29.opExtrude","SWEPT_EDGE",EDGE,{"disambiguationData":[OSD([subQ0,subQ1])]})});}
            var Q25;
            {var subQ0=sQuery(id+"F28.wireOp",EDGE,"E131.right");var subQ1=sQuery(id+"F28.wireOp",EDGE,"E131.top");Q25=makeQuery(id+"F29.boolean.opBoolean","COPY",EDGE,{"disambiguationData":[TD([makeQuery(id+"F10.boolean.opBoolean","COPY",FACE,{"derivedFrom":makeQuery(id+"F10.opExtrude","SWEPT_FACE",FACE,{"disambiguationData":[OSD([sQuery(id+"F8.wireOp",EDGE,"E115.MirrorCS")])]})})])],"derivedFrom":makeQuery(id+"F29.opExtrude","SWEPT_EDGE",EDGE,{"disambiguationData":[OSD([subQ1,subQ0])]})});}
            var Q26;
            {var subQ0=sQuery(id+"F28.wireOp",EDGE,"E134.top");var subQ1=sQuery(id+"F28.wireOp",EDGE,"E134.right");Q26=makeQuery(id+"F29.boolean.opBoolean","COPY",EDGE,{"disambiguationData":[TD([makeQuery(id+"F9.boolean.opBoolean","COPY",FACE,{"derivedFrom":makeQuery(id+"F9.opExtrude","SWEPT_FACE",FACE,{"disambiguationData":[OSD([sQuery(id+"F5.wireOp",EDGE,"E34.MirrorCS")])]})})])],"derivedFrom":makeQuery(id+"F29.opExtrude","SWEPT_EDGE",EDGE,{"disambiguationData":[OSD([subQ0,subQ1])]})});}
            var Q27;
            {var subQ0=sQuery(id+"F28.wireOp",EDGE,"E133.top");var subQ1=sQuery(id+"F28.wireOp",EDGE,"E133.right");Q27=makeQuery(id+"F29.boolean.opBoolean","COPY",EDGE,{"disambiguationData":[TD([makeQuery(id+"F9.boolean.opBoolean","COPY",FACE,{"derivedFrom":makeQuery(id+"F9.opExtrude","SWEPT_FACE",FACE,{"disambiguationData":[OSD([sQuery(id+"F5.wireOp",EDGE,"E31.MirrorCS")])]})})])],"derivedFrom":makeQuery(id+"F29.opExtrude","SWEPT_EDGE",EDGE,{"disambiguationData":[OSD([subQ0,subQ1])]})});}
            var Q28;
            {var subQ0=sQuery(id+"F28.wireOp",EDGE,"E132.top");var subQ1=sQuery(id+"F28.wireOp",EDGE,"E132.right");Q28=makeQuery(id+"F29.boolean.opBoolean","COPY",EDGE,{"disambiguationData":[TD([makeQuery(id+"F9.boolean.opBoolean","COPY",FACE,{"derivedFrom":makeQuery(id+"F9.opExtrude","SWEPT_FACE",FACE,{"disambiguationData":[OSD([sQuery(id+"F5.wireOp",EDGE,"E29.top"),sQuery(id+"F5.wireOp",EDGE,"E32.MirrorCS"),sQuery(id+"F5.wireOp",EDGE,"E44")])]})})])],"derivedFrom":makeQuery(id+"F29.opExtrude","SWEPT_EDGE",EDGE,{"disambiguationData":[OSD([subQ0,subQ1])]})});}
            var Q29;
            {var subQ0=sQuery(id+"F28.wireOp",EDGE,"E133.right");var subQ1=sQuery(id+"F28.wireOp",EDGE,"E133.top");Q29=makeQuery(id+"F29.boolean.opBoolean","COPY",EDGE,{"disambiguationData":[TD([makeQuery(id+"F9.boolean.opBoolean","COPY",FACE,{"derivedFrom":makeQuery(id+"F9.opExtrude","SWEPT_FACE",FACE,{"disambiguationData":[OSD([sQuery(id+"F5.wireOp",EDGE,"E29.top"),sQuery(id+"F5.wireOp",EDGE,"E32.MirrorCS"),sQuery(id+"F5.wireOp",EDGE,"E44")])]})})])],"derivedFrom":makeQuery(id+"F29.opExtrude","SWEPT_EDGE",EDGE,{"disambiguationData":[OSD([subQ1,subQ0])]})});}
            var Q30;
            {var subQ0=sQuery(id+"F28.wireOp",EDGE,"E134.top");var subQ1=sQuery(id+"F28.wireOp",EDGE,"E134.right");Q30=makeQuery(id+"F29.boolean.opBoolean","COPY",EDGE,{"disambiguationData":[TD([makeQuery(id+"F9.boolean.opBoolean","COPY",FACE,{"derivedFrom":makeQuery(id+"F9.opExtrude","SWEPT_FACE",FACE,{"disambiguationData":[OSD([sQuery(id+"F5.wireOp",EDGE,"E29.top"),sQuery(id+"F5.wireOp",EDGE,"E32.MirrorCS"),sQuery(id+"F5.wireOp",EDGE,"E44")])]})})])],"derivedFrom":makeQuery(id+"F29.opExtrude","SWEPT_EDGE",EDGE,{"disambiguationData":[OSD([subQ0,subQ1])]})});}
            var Q31;
            {var subQ0=sQuery(id+"F28.wireOp",EDGE,"E131.top");var subQ1=sQuery(id+"F28.wireOp",EDGE,"E131.right");Q31=makeQuery(id+"F29.boolean.opBoolean","COPY",EDGE,{"disambiguationData":[TD([makeQuery(id+"F9.boolean.opBoolean","COPY",FACE,{"derivedFrom":makeQuery(id+"F9.opExtrude","SWEPT_FACE",FACE,{"disambiguationData":[OSD([sQuery(id+"F5.wireOp",EDGE,"E29.top"),sQuery(id+"F5.wireOp",EDGE,"E32.MirrorCS"),sQuery(id+"F5.wireOp",EDGE,"E44")])]})})])],"derivedFrom":makeQuery(id+"F29.opExtrude","SWEPT_EDGE",EDGE,{"disambiguationData":[OSD([subQ0,subQ1])]})});}
            chamfer(context, id + "F33", {"entities" : qUnion([Q0, Q1, Q2, Q3, Q4, Q5, Q6, Q7, Q8, Q9, Q10, Q11, Q12, Q13, Q14, Q15, Q16, Q17, Q18, Q19, Q20, Q21, Q22, Q23, Q24, Q25, Q26, Q27, Q28, Q29, Q30, Q31]), "width" : 0.8 * mm, "tangentPropagation" : true});
        }
        {
            var Q0;
            {var subQ0=sQuery(id+"F0.wireOp",EDGE,"E0.left");Q0=makeQuery(id+"F29.boolean.opBoolean","SPLIT",FACE,{"disambiguationData":[TD([makeQuery(id+"F9.boolean.opBoolean","COPY",FACE,{"derivedFrom":makeQuery(id+"F9.opExtrude","SWEPT_FACE",FACE,{"disambiguationData":[OSD([sQuery(id+"F5.wireOp",EDGE,"E28.1")])]})})])],"derivedFrom":makeQuery(id+"F1.opExtrude","SWEPT_FACE",FACE,{"disambiguationData":[OSD([subQ0])]})});}
            var sketch = newSketch(context, id + "F34", { "sketchPlane" : qUnion([Q0])});
            skLineSegment(sketch, "E135.bottom", {"start": v(-150.11, 77.75) * mm, "end": v(173.18, 77.75) * mm});
            skLineSegment(sketch, "E135.top", {"start": v(-150.11, -50.8) * mm, "end": v(173.18, -50.8) * mm});
            skLineSegment(sketch, "E135.left", {"start": v(-150.11, 77.75) * mm, "end": v(-150.11, -50.8) * mm});
            skLineSegment(sketch, "E135.right", {"start": v(173.18, 77.75) * mm, "end": v(173.18, -50.8) * mm});
            skSolve(sketch);
        }
        {
            var Q0;
            Q0=makeQuery(id+"F34.imprint","IMPRINT",FACE,{"disambiguationData":[TD([[makeQuery(id+"F34.imprint","IMPRINT",EDGE,{"derivedFrom":sQuery(id+"F34.wireOp",EDGE,"E135.bottom")}),-1.0]])]});
            extrude(context, id + "F35", {"entities" : qUnion([Q0]), "operationType" : NewBodyOperationType.REMOVE, "oppositeDirection" : true, "depth" : 127 * mm, "offsetDistance" : 25.4 * mm});
        }
    });
